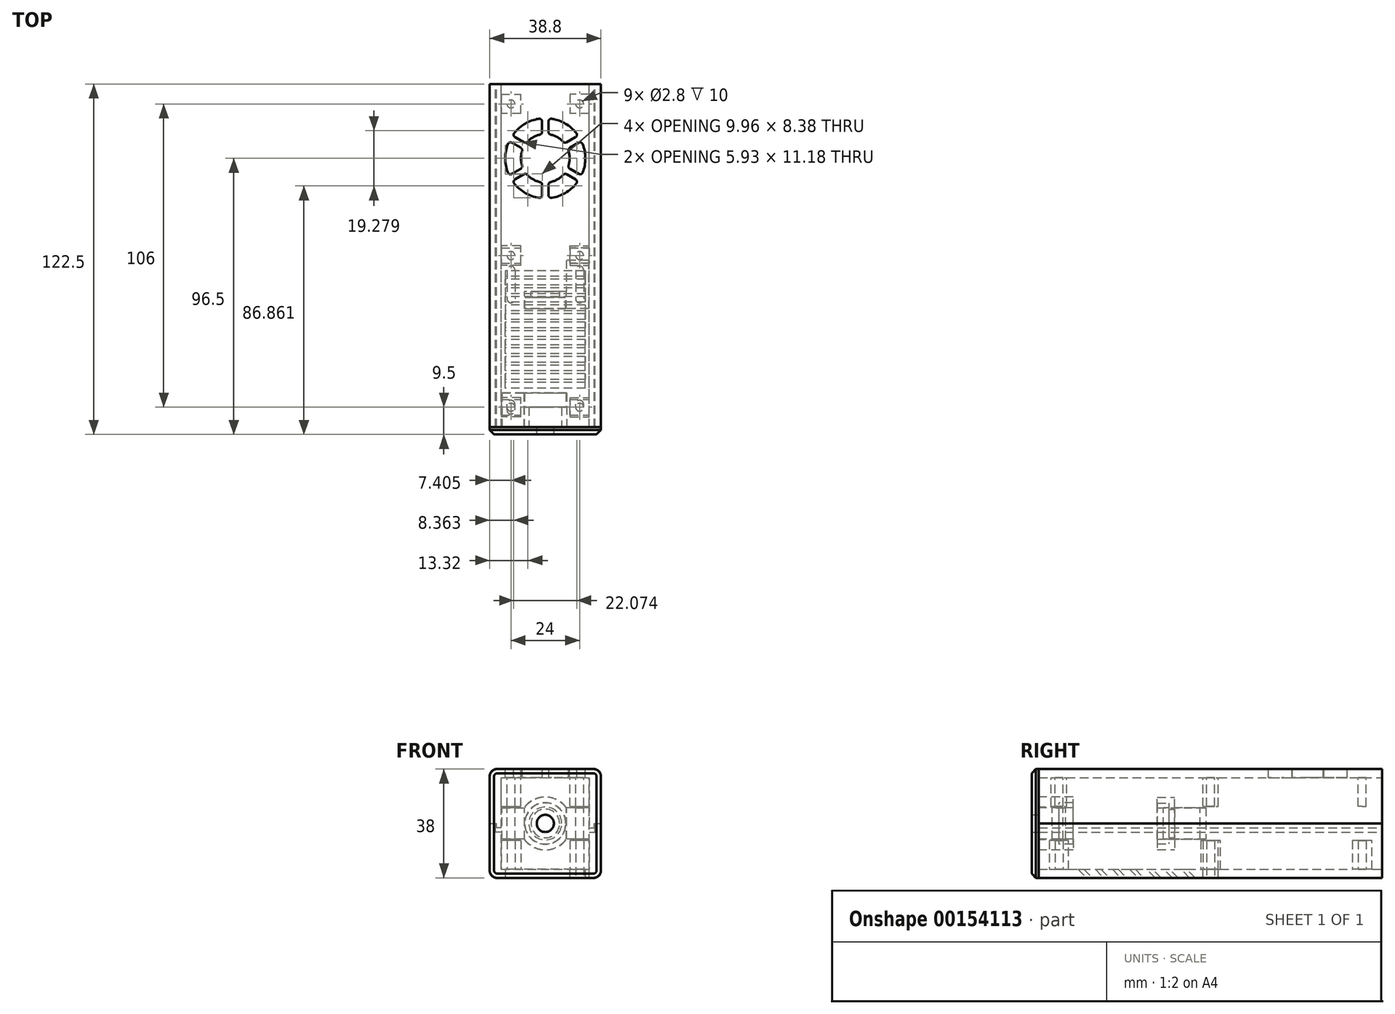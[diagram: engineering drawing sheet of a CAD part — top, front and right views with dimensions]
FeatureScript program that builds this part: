
annotation { "Feature Type Name" : "Feature", "Feature Type Description" : "" }
export const myFeature = defineFeature(function(context is Context, id is Id, definition is map)
    precondition{}
    {
        {
            var Q0;
            Q0=qCreatedBy(makeId("Front.planeOp"),FACE);
            var sketch = newSketch(context, id + "F0", { "sketchPlane" : qUnion([Q0])});
            skLineSegment(sketch, "E0", {"start": v(-19.4, 0) * mm, "end": v(-19.4, -16.6) * mm});
            skLineSegment(sketch, "E1", {"start": v(-17, -19) * mm, "end": v(0, -19) * mm});
            skLineSegment(sketch, "E2", {"start": v(10, -16) * mm, "end": v(-15.4, -16) * mm});
            skLineSegment(sketch, "E3", {"start": v(-15.4, -16) * mm, "end": v(-15.4, -3) * mm});
            skLineSegment(sketch, "E4", {"start": v(-15.4, -3) * mm, "end": v(-17.4, -3) * mm});
            skLineSegment(sketch, "E5", {"start": v(-17.4, -3) * mm, "end": v(-17.4, 0) * mm});
            skPoint(sketch, "E6.visualSharp", {"position": v(-19.4, -19) * mm});
            skArc(sketch, "E6.filletArc", {"start": v(-19.4, -16.6) * mm, "mid": v(-18.7, -18.3) * mm, "end": v(-17, -19) * mm});
            skLineSegment(sketch, "E7.MirrorCS", {"start": v(17.4, 0) * mm, "end": v(19.4, 0) * mm});
            skLineSegment(sketch, "E8.MirrorCS", {"start": v(15.4, -3) * mm, "end": v(17.4, -3) * mm});
            skLineSegment(sketch, "E9.MirrorCS", {"start": v(19.4, 0) * mm, "end": v(19.4, -16.6) * mm});
            skLineSegment(sketch, "E10.MirrorCS", {"start": v(-10, -16) * mm, "end": v(15.4, -16) * mm});
            skLineSegment(sketch, "E11.MirrorCS", {"start": v(17.4, -3) * mm, "end": v(17.4, 0) * mm});
            skLineSegment(sketch, "E12.MirrorCS", {"start": v(15.4, -16) * mm, "end": v(15.4, -3) * mm});
            skLineSegment(sketch, "E13.MirrorCS", {"start": v(17, -19) * mm, "end": v(0, -19) * mm});
            skPoint(sketch, "E14.MirrorP", {"position": v(19.4, -19) * mm});
            skArc(sketch, "E15.MirrorCS", {"start": v(19.4, -16.6) * mm, "mid": v(18.7, -18.3) * mm, "end": v(17, -19) * mm});
            skLineSegment(sketch, "E16.MirrorCS", {"start": v(-17, 19) * mm, "end": v(0, 19) * mm});
            skLineSegment(sketch, "E17.MirrorCS", {"start": v(17, 19) * mm, "end": v(0, 19) * mm});
            skArc(sketch, "E18.MirrorCS", {"start": v(19.4, 16.6) * mm, "mid": v(18.7, 18.3) * mm, "end": v(17, 19) * mm});
            skLineSegment(sketch, "E19.MirrorCS", {"start": v(19.4, 0) * mm, "end": v(19.4, 16.6) * mm});
            skLineSegment(sketch, "E20.MirrorCS", {"start": v(-19.4, 0) * mm, "end": v(-19.4, 16.6) * mm});
            skPoint(sketch, "E21.MirrorP", {"position": v(-19.4, 19) * mm});
            skArc(sketch, "E22.MirrorCS", {"start": v(-19.4, 16.6) * mm, "mid": v(-18.7, 18.3) * mm, "end": v(-17, 19) * mm});
            skLineSegment(sketch, "E23", {"start": v(-19.4, 0) * mm, "end": v(-17.4, 0) * mm});
            skLineSegment(sketch, "E24", {"start": v(-15.4, -1.5) * mm, "end": v(-15.4, 16) * mm});
            skLineSegment(sketch, "E25", {"start": v(-15.4, -1.5) * mm, "end": v(-17.1, -1.5) * mm});
            skLineSegment(sketch, "E26", {"start": v(-17.1, -1.5) * mm, "end": v(-17.1, 0) * mm});
            skLineSegment(sketch, "E27", {"start": v(-17.1, 0) * mm, "end": v(-17.4, 0) * mm});
            skLineSegment(sketch, "E28", {"start": v(-15.4, 16) * mm, "end": v(15.4, 16) * mm});
            skLineSegment(sketch, "E29", {"start": v(15.4, 16) * mm, "end": v(15.4, -1.5) * mm});
            skLineSegment(sketch, "E30", {"start": v(15.4, -1.5) * mm, "end": v(17.1, -1.5) * mm});
            skPoint(sketch, "E30.endSnap0", {"position": v(17.4, -1.5) * mm});
            skLineSegment(sketch, "E31", {"start": v(17.1, -1.5) * mm, "end": v(17.1, 0) * mm});
            skLineSegment(sketch, "E32", {"start": v(17.1, 0) * mm, "end": v(17.4, 0) * mm});
            skSolve(sketch);
        }
        {
            var Q0;
            Q0=makeQuery(id+"F0.imprint","IMPRINT",FACE,{"disambiguationData":[TD([[makeQuery(id+"F0.imprint","IMPRINT",EDGE,{"derivedFrom":sQuery(id+"F0.wireOp",EDGE,"E0")}),1.0]])]});
            var Q1;
            {var subQ0=sQuery(id+"F0.wireOp",EDGE,"Xo03iRkJ-jKT7-Ic2D-cY5B-pt2Z7VC4vIDv");Q1=makeQuery(id+"F0.imprint","IMPRINT",FACE,{"disambiguationData":[TD([[makeQuery(id+"F0.imprint","IMPRINT",EDGE,{"derivedFrom":subQ0}),-1.0]])]});}
            var Q2;
            {var subQ0=sQuery(id+"F0.wireOp",EDGE,"d39963a0-51db-4fea-9cc0-66fd8d7172660.MirrorCS");Q2=makeQuery(id+"F0.imprint","IMPRINT",FACE,{"disambiguationData":[TD([[makeQuery(id+"F0.imprint","IMPRINT",EDGE,{"derivedFrom":subQ0}),1.0]])]});}
            extrude(context, id + "F1", {"entities" : qUnion([Q0, Q1, Q2]), "depth" : 60 * mm, "hasSecondDirection" : true, "secondDirectionOppositeDirection" : true, "secondDirectionDepth" : 60 * mm});
        }
        {
            var Q0;
            Q0=makeQuery(id+"F0.imprint","IMPRINT",FACE,{"disambiguationData":[TD([[makeQuery(id+"F0.imprint","IMPRINT",EDGE,{"derivedFrom":sQuery(id+"F0.wireOp",EDGE,"E7.MirrorCS")}),1.0]])]});
            var Q1;
            {var subQ0=sQuery(id+"F0.wireOp",EDGE,"ff36f887-7d90-4820-9e64-af2514271e780.MirrorCS");Q1=makeQuery(id+"F0.imprint","IMPRINT",FACE,{"disambiguationData":[TD([[makeQuery(id+"F0.imprint","IMPRINT",EDGE,{"derivedFrom":subQ0}),1.0]])]});}
            var Q2;
            {var subQ0=sQuery(id+"F0.wireOp",EDGE,"acc9a72e-b05e-4517-aa3a-cfba1e2fd8f90.MirrorCS");Q2=makeQuery(id+"F0.imprint","IMPRINT",FACE,{"disambiguationData":[TD([[makeQuery(id+"F0.imprint","IMPRINT",EDGE,{"derivedFrom":subQ0}),-1.0]])]});}
            var Q3;
            Q3=makeQuery(id+"F1.opExtrude","CAP_FACE",FACE,{"disambiguationData":[OSD([sQuery(id+"F0.wireOp",EDGE,"E0"),sQuery(id+"F0.wireOp",EDGE,"E1"),sQuery(id+"F0.wireOp",EDGE,"E2"),sQuery(id+"F0.wireOp",EDGE,"E3"),sQuery(id+"F0.wireOp",EDGE,"E4"),sQuery(id+"F0.wireOp",EDGE,"E5"),sQuery(id+"F0.wireOp",EDGE,"E6.filletArc"),sQuery(id+"F0.wireOp",EDGE,"E7.MirrorCS"),sQuery(id+"F0.wireOp",EDGE,"E8.MirrorCS"),sQuery(id+"F0.wireOp",EDGE,"E9.MirrorCS"),sQuery(id+"F0.wireOp",EDGE,"E10.MirrorCS"),sQuery(id+"F0.wireOp",EDGE,"E11.MirrorCS"),sQuery(id+"F0.wireOp",EDGE,"E12.MirrorCS"),sQuery(id+"F0.wireOp",EDGE,"E13.MirrorCS"),sQuery(id+"F0.wireOp",EDGE,"E15.MirrorCS"),sQuery(id+"F0.wireOp",EDGE,"Xo03iRkJ-jKT7-Ic2D-cY5B-pt2Z7VC4vIDv"),sQuery(id+"F0.wireOp",EDGE,"BTEHV5c4-qzld-xg7n-A6UV-d1dODqSnIxqR"),sQuery(id+"F0.wireOp",EDGE,"j2f2Hjq2-E5bA-Y5t0-WPVC-FpMQT2KFEy1b"),sQuery(id+"F0.wireOp",EDGE,"d39963a0-51db-4fea-9cc0-66fd8d7172660.MirrorCS"),sQuery(id+"F0.wireOp",EDGE,"d39963a0-51db-4fea-9cc0-66fd8d7172661.MirrorCS"),sQuery(id+"F0.wireOp",EDGE,"d39963a0-51db-4fea-9cc0-66fd8d7172662.MirrorCS"),sQuery(id+"F0.wireOp",EDGE,"E23")])],"isStart":false});
            var Q4;
            Q4=makeQuery(id+"F1.opExtrude","CAP_FACE",FACE,{"disambiguationData":[OSD([sQuery(id+"F0.wireOp",EDGE,"E0"),sQuery(id+"F0.wireOp",EDGE,"E1"),sQuery(id+"F0.wireOp",EDGE,"E2"),sQuery(id+"F0.wireOp",EDGE,"E3"),sQuery(id+"F0.wireOp",EDGE,"E4"),sQuery(id+"F0.wireOp",EDGE,"E5"),sQuery(id+"F0.wireOp",EDGE,"E6.filletArc"),sQuery(id+"F0.wireOp",EDGE,"E7.MirrorCS"),sQuery(id+"F0.wireOp",EDGE,"E8.MirrorCS"),sQuery(id+"F0.wireOp",EDGE,"E9.MirrorCS"),sQuery(id+"F0.wireOp",EDGE,"E10.MirrorCS"),sQuery(id+"F0.wireOp",EDGE,"E11.MirrorCS"),sQuery(id+"F0.wireOp",EDGE,"E12.MirrorCS"),sQuery(id+"F0.wireOp",EDGE,"E13.MirrorCS"),sQuery(id+"F0.wireOp",EDGE,"E15.MirrorCS"),sQuery(id+"F0.wireOp",EDGE,"Xo03iRkJ-jKT7-Ic2D-cY5B-pt2Z7VC4vIDv"),sQuery(id+"F0.wireOp",EDGE,"BTEHV5c4-qzld-xg7n-A6UV-d1dODqSnIxqR"),sQuery(id+"F0.wireOp",EDGE,"j2f2Hjq2-E5bA-Y5t0-WPVC-FpMQT2KFEy1b"),sQuery(id+"F0.wireOp",EDGE,"d39963a0-51db-4fea-9cc0-66fd8d7172660.MirrorCS"),sQuery(id+"F0.wireOp",EDGE,"d39963a0-51db-4fea-9cc0-66fd8d7172661.MirrorCS"),sQuery(id+"F0.wireOp",EDGE,"d39963a0-51db-4fea-9cc0-66fd8d7172662.MirrorCS"),sQuery(id+"F0.wireOp",EDGE,"E23")])],"isStart":true});
            extrude(context, id + "F2", {"entities" : qUnion([Q0, Q1, Q2]), "endBound" : BoundingType.UP_TO_SURFACE, "endBoundEntityFace" : qUnion([Q3]), "depth" : 25 * mm, "hasSecondDirection" : true, "secondDirectionBound" : SecondDirectionBoundingType.UP_TO_SURFACE, "secondDirectionOppositeDirection" : true, "secondDirectionBoundEntityFace" : qUnion([Q4]), "secondDirectionDepth" : 25 * mm});
        }
        {
            var Q0;
            {var subQ0=sQuery(id+"F0.wireOp",EDGE,"E10.MirrorCS");Q0=makeQuery(id+"F1.opExtrude","SWEPT_FACE",FACE,{"disambiguationData":[OSD([subQ0]),TDD([makeQuery(id+"F0.imprint","IMPRINT",EDGE,{"disambiguationData":[TD([[makeQuery(id+"F0.imprint","INTERSECT",VERTEX,{"derivedFrom":[subQ0,sQuery(id+"F0.wireOp",EDGE,"E12.MirrorCS")]}),1.0]])],"derivedFrom":subQ0})])]});}
            cPlane(context, id + "F3", {"entities" : qUnion([Q0]), "cplaneType" : CPlaneType.OFFSET, "offset" : 0 * mm, "width" : 150 * mm, "height" : 150 * mm});
        }
        {
            var Q0;
            Q0=qCreatedBy(id+"F3.planeOp",FACE);
            var sketch = newSketch(context, id + "F4", { "sketchPlane" : qUnion([Q0])});
            skLineSegment(sketch, "E33", {"start": v(10.01, 0) * mm, "end": v(15.4, 0) * mm, "construction": true});
            skLineSegment(sketch, "E34.bottom", {"start": v(15.4, 2.7) * mm, "end": v(10, 2.7) * mm});
            skLineSegment(sketch, "E34.top", {"start": v(15.4, -2.7) * mm, "end": v(10, -2.7) * mm});
            skLineSegment(sketch, "E34.left", {"start": v(15.4, 2.7) * mm, "end": v(15.4, -2.7) * mm});
            skPoint(sketch, "E34.middle", {"position": v(12, 0) * mm});
            skCircle(sketch, "E35", {"center": v(12, 0) * mm, "radius": 1.4 * mm});
            skLineSegment(sketch, "E36.MirrorCS", {"start": v(15.4, -2.7) * mm, "end": v(15.4, 2.7) * mm});
            skLineSegment(sketch, "E37.bottom", {"start": v(10, 2.7) * mm, "end": v(8.6, 2.7) * mm});
            skLineSegment(sketch, "E37.top", {"start": v(10, -2.7) * mm, "end": v(8.6, -2.7) * mm});
            skLineSegment(sketch, "E37.right", {"start": v(8.6, 2.7) * mm, "end": v(8.6, -2.7) * mm});
            skPoint(sketch, "E38.0.1.0", {"position": v(12, 53) * mm});
            skLineSegment(sketch, "E38.0.1.1", {"start": v(10.01, 53) * mm, "end": v(15.4, 53) * mm, "construction": true});
            skCircle(sketch, "E38.0.1.2", {"center": v(12, 53) * mm, "radius": 1.4 * mm});
            skLineSegment(sketch, "E38.0.1.3", {"start": v(15.4, 55.7) * mm, "end": v(10, 55.7) * mm});
            skLineSegment(sketch, "E38.0.1.4", {"start": v(15.4, 50.3) * mm, "end": v(15.4, 55.7) * mm});
            skLineSegment(sketch, "E38.0.1.5", {"start": v(8.6, 55.7) * mm, "end": v(8.6, 50.3) * mm});
            skPoint(sketch, "E38.0.1.6", {"position": v(12, 53) * mm});
            skLineSegment(sketch, "E38.0.1.7", {"start": v(15.4, 55.7) * mm, "end": v(10, 55.7) * mm});
            skLineSegment(sketch, "E38.0.1.8", {"start": v(15.4, 55.7) * mm, "end": v(15.4, 50.3) * mm});
            skCircle(sketch, "E38.0.1.9", {"center": v(12, 53) * mm, "radius": 1.4 * mm});
            skLineSegment(sketch, "E38.0.1.10", {"start": v(15.4, 50.3) * mm, "end": v(10, 50.3) * mm});
            skLineSegment(sketch, "E38.0.1.11", {"start": v(15.4, 50.3) * mm, "end": v(10, 50.3) * mm});
            skLineSegment(sketch, "E38.0.1.12", {"start": v(10, 55.7) * mm, "end": v(8.6, 55.7) * mm});
            skLineSegment(sketch, "E38.0.1.13", {"start": v(10, 50.3) * mm, "end": v(8.6, 50.3) * mm});
            skPoint(sketch, "E38.1.0.0", {"position": v(-12, 0) * mm});
            skLineSegment(sketch, "E38.1.0.1", {"start": v(-13.99, 0) * mm, "end": v(-8.6, 0) * mm, "construction": true});
            skCircle(sketch, "E38.1.0.2", {"center": v(-12, 0) * mm, "radius": 1.4 * mm});
            skLineSegment(sketch, "E38.1.0.3", {"start": v(-8.6, 2.7) * mm, "end": v(-14, 2.7) * mm});
            skLineSegment(sketch, "E38.1.0.4", {"start": v(-8.6, -2.7) * mm, "end": v(-8.6, 2.7) * mm});
            skLineSegment(sketch, "E38.1.0.5", {"start": v(-15.4, 2.7) * mm, "end": v(-15.4, -2.7) * mm});
            skPoint(sketch, "E38.1.0.6", {"position": v(-12, 0) * mm});
            skLineSegment(sketch, "E38.1.0.7", {"start": v(-8.6, 2.7) * mm, "end": v(-14, 2.7) * mm});
            skLineSegment(sketch, "E38.1.0.8", {"start": v(-8.6, 2.7) * mm, "end": v(-8.6, -2.7) * mm});
            skCircle(sketch, "E38.1.0.9", {"center": v(-12, 0) * mm, "radius": 1.4 * mm});
            skLineSegment(sketch, "E38.1.0.10", {"start": v(-8.6, -2.7) * mm, "end": v(-14, -2.7) * mm});
            skLineSegment(sketch, "E38.1.0.11", {"start": v(-8.6, -2.7) * mm, "end": v(-14, -2.7) * mm});
            skLineSegment(sketch, "E38.1.0.12", {"start": v(-14, 2.7) * mm, "end": v(-15.4, 2.7) * mm});
            skLineSegment(sketch, "E38.1.0.13", {"start": v(-14, -2.7) * mm, "end": v(-15.4, -2.7) * mm});
            skPoint(sketch, "E38.1.1.0", {"position": v(-12, 53) * mm});
            skLineSegment(sketch, "E38.1.1.1", {"start": v(-13.99, 53) * mm, "end": v(-8.6, 53) * mm, "construction": true});
            skCircle(sketch, "E38.1.1.2", {"center": v(-12, 53) * mm, "radius": 1.4 * mm});
            skLineSegment(sketch, "E38.1.1.3", {"start": v(-8.6, 55.7) * mm, "end": v(-14, 55.7) * mm});
            skLineSegment(sketch, "E38.1.1.4", {"start": v(-8.6, 50.3) * mm, "end": v(-8.6, 55.7) * mm});
            skLineSegment(sketch, "E38.1.1.5", {"start": v(-15.4, 55.7) * mm, "end": v(-15.4, 50.3) * mm});
            skPoint(sketch, "E38.1.1.6", {"position": v(-12, 53) * mm});
            skLineSegment(sketch, "E38.1.1.7", {"start": v(-8.6, 55.7) * mm, "end": v(-14, 55.7) * mm});
            skLineSegment(sketch, "E38.1.1.8", {"start": v(-8.6, 55.7) * mm, "end": v(-8.6, 50.3) * mm});
            skCircle(sketch, "E38.1.1.9", {"center": v(-12, 53) * mm, "radius": 1.4 * mm});
            skLineSegment(sketch, "E38.1.1.10", {"start": v(-8.6, 50.3) * mm, "end": v(-14, 50.3) * mm});
            skLineSegment(sketch, "E38.1.1.11", {"start": v(-8.6, 50.3) * mm, "end": v(-14, 50.3) * mm});
            skLineSegment(sketch, "E38.1.1.12", {"start": v(-14, 55.7) * mm, "end": v(-15.4, 55.7) * mm});
            skLineSegment(sketch, "E38.1.1.13", {"start": v(-14, 50.3) * mm, "end": v(-15.4, 50.3) * mm});
            skLineSegment(sketch, "E38.direction1", {"start": v(8.6, -2.7) * mm, "end": v(-15.4, -2.7) * mm, "construction": true});
            skLineSegment(sketch, "E38.direction2", {"start": v(8.6, -2.7) * mm, "end": v(8.6, 50.3) * mm, "construction": true});
            skPoint(sketch, "E39.0.1.0", {"position": v(12, -53) * mm});
            skLineSegment(sketch, "E39.0.1.1", {"start": v(8.6, -55.7) * mm, "end": v(-15.4, -55.7) * mm, "construction": true});
            skPoint(sketch, "E39.0.1.2", {"position": v(-12, -53) * mm});
            skPoint(sketch, "E39.0.1.3", {"position": v(12, -53) * mm});
            skPoint(sketch, "E39.0.1.4", {"position": v(-12, -53) * mm});
            skLineSegment(sketch, "E39.0.1.5", {"start": v(-14, -55.7) * mm, "end": v(-15.4, -55.7) * mm});
            skLineSegment(sketch, "E39.0.1.6", {"start": v(8.6, -50.3) * mm, "end": v(8.6, -55.7) * mm});
            skLineSegment(sketch, "E39.0.1.7", {"start": v(-8.6, -55.7) * mm, "end": v(-14, -55.7) * mm});
            skLineSegment(sketch, "E39.0.1.8", {"start": v(-15.4, -50.3) * mm, "end": v(-15.4, -55.7) * mm});
            skLineSegment(sketch, "E39.0.1.9", {"start": v(15.4, -55.7) * mm, "end": v(10, -55.7) * mm});
            skLineSegment(sketch, "E39.0.1.10", {"start": v(15.4, -50.3) * mm, "end": v(10, -50.3) * mm});
            skLineSegment(sketch, "E39.0.1.11", {"start": v(-14, -50.3) * mm, "end": v(-15.4, -50.3) * mm});
            skLineSegment(sketch, "E39.0.1.12", {"start": v(10.01, -53) * mm, "end": v(15.4, -53) * mm, "construction": true});
            skCircle(sketch, "E39.0.1.13", {"center": v(12, -53) * mm, "radius": 1.4 * mm});
            skLineSegment(sketch, "E39.0.1.14", {"start": v(15.4, -55.7) * mm, "end": v(15.4, -50.3) * mm});
            skLineSegment(sketch, "E39.0.1.15", {"start": v(10, -50.3) * mm, "end": v(8.6, -50.3) * mm});
            skLineSegment(sketch, "E39.0.1.16", {"start": v(10, -55.7) * mm, "end": v(8.6, -55.7) * mm});
            skLineSegment(sketch, "E39.0.1.17", {"start": v(-8.6, -55.7) * mm, "end": v(-8.6, -50.3) * mm});
            skLineSegment(sketch, "E39.0.1.18", {"start": v(-8.6, -50.3) * mm, "end": v(-14, -50.3) * mm});
            skLineSegment(sketch, "E39.0.1.19", {"start": v(-13.99, -53) * mm, "end": v(-8.6, -53) * mm, "construction": true});
            skLineSegment(sketch, "E39.0.1.20", {"start": v(-8.6, -55.7) * mm, "end": v(-14, -55.7) * mm});
            skCircle(sketch, "E39.0.1.21", {"center": v(-12, -53) * mm, "radius": 1.4 * mm});
            skLineSegment(sketch, "E39.0.1.22", {"start": v(-8.6, -50.3) * mm, "end": v(-14, -50.3) * mm});
            skLineSegment(sketch, "E39.0.1.23", {"start": v(15.4, -50.3) * mm, "end": v(10, -50.3) * mm});
            skLineSegment(sketch, "E39.0.1.24", {"start": v(15.4, -55.7) * mm, "end": v(10, -55.7) * mm});
            skLineSegment(sketch, "E39.0.1.25", {"start": v(15.4, -50.3) * mm, "end": v(15.4, -55.7) * mm});
            skCircle(sketch, "E39.0.1.26", {"center": v(12, -53) * mm, "radius": 1.4 * mm});
            skLineSegment(sketch, "E39.0.1.27", {"start": v(-8.6, -50.3) * mm, "end": v(-8.6, -55.7) * mm});
            skCircle(sketch, "E39.0.1.28", {"center": v(-12, -53) * mm, "radius": 1.4 * mm});
            skLineSegment(sketch, "E39.direction1", {"start": v(-15.4, -2.7) * mm, "end": v(74.5, -2.7) * mm, "construction": true});
            skLineSegment(sketch, "E39.direction2", {"start": v(-15.4, -2.7) * mm, "end": v(-15.4, -55.7) * mm, "construction": true});
            skLineSegment(sketch, "E40.bottom", {"start": v(-8.6, 2.7) * mm, "end": v(-15.4, 2.7) * mm});
            skLineSegment(sketch, "E40.top", {"start": v(-8.6, 3.4) * mm, "end": v(-15.4, 3.4) * mm});
            skLineSegment(sketch, "E40.left", {"start": v(-8.6, 2.7) * mm, "end": v(-8.6, 3.4) * mm});
            skLineSegment(sketch, "E40.right", {"start": v(-15.4, 2.7) * mm, "end": v(-15.4, 3.4) * mm});
            skLineSegment(sketch, "E41.bottom", {"start": v(-8.6, -2.7) * mm, "end": v(-15.4, -2.7) * mm});
            skLineSegment(sketch, "E41.top", {"start": v(-8.6, -3.4) * mm, "end": v(-15.4, -3.4) * mm});
            skLineSegment(sketch, "E41.left", {"start": v(-8.6, -2.7) * mm, "end": v(-8.6, -3.4) * mm});
            skLineSegment(sketch, "E41.right", {"start": v(-15.4, -2.7) * mm, "end": v(-15.4, -3.4) * mm});
            skLineSegment(sketch, "E42.bottom", {"start": v(8.6, -2.7) * mm, "end": v(15.4, -2.7) * mm});
            skLineSegment(sketch, "E42.top", {"start": v(8.6, -3.4) * mm, "end": v(15.4, -3.4) * mm});
            skLineSegment(sketch, "E42.left", {"start": v(8.6, -2.7) * mm, "end": v(8.6, -3.4) * mm});
            skLineSegment(sketch, "E42.right", {"start": v(15.4, -2.7) * mm, "end": v(15.4, -3.4) * mm});
            skLineSegment(sketch, "E43.bottom", {"start": v(8.6, 2.7) * mm, "end": v(15.4, 2.7) * mm});
            skLineSegment(sketch, "E43.top", {"start": v(8.6, 3.4) * mm, "end": v(15.4, 3.4) * mm});
            skLineSegment(sketch, "E43.left", {"start": v(8.6, 2.7) * mm, "end": v(8.6, 3.4) * mm});
            skLineSegment(sketch, "E43.right", {"start": v(15.4, 2.7) * mm, "end": v(15.4, 3.4) * mm});
            skLineSegment(sketch, "E44.bottom", {"start": v(-8.6, 50.3) * mm, "end": v(-15.4, 50.3) * mm});
            skLineSegment(sketch, "E44.top", {"start": v(-8.6, 49.6) * mm, "end": v(-15.4, 49.6) * mm});
            skLineSegment(sketch, "E44.left", {"start": v(-8.6, 50.3) * mm, "end": v(-8.6, 49.6) * mm});
            skLineSegment(sketch, "E44.right", {"start": v(-15.4, 50.3) * mm, "end": v(-15.4, 49.6) * mm});
            skLineSegment(sketch, "E45.bottom", {"start": v(15.4, 50.3) * mm, "end": v(8.6, 50.3) * mm});
            skLineSegment(sketch, "E45.top", {"start": v(15.4, 49.6) * mm, "end": v(8.6, 49.6) * mm});
            skLineSegment(sketch, "E45.left", {"start": v(15.4, 50.3) * mm, "end": v(15.4, 49.6) * mm});
            skLineSegment(sketch, "E45.right", {"start": v(8.6, 50.3) * mm, "end": v(8.6, 49.6) * mm});
            skLineSegment(sketch, "E46.bottom", {"start": v(15.4, 55.7) * mm, "end": v(8.6, 55.7) * mm});
            skLineSegment(sketch, "E46.top", {"start": v(15.4, 56.4) * mm, "end": v(8.6, 56.4) * mm});
            skLineSegment(sketch, "E46.left", {"start": v(15.4, 55.7) * mm, "end": v(15.4, 56.4) * mm});
            skLineSegment(sketch, "E46.right", {"start": v(8.6, 55.7) * mm, "end": v(8.6, 56.4) * mm});
            skLineSegment(sketch, "E47.bottom", {"start": v(-15.4, 55.7) * mm, "end": v(-8.6, 55.7) * mm});
            skLineSegment(sketch, "E47.top", {"start": v(-15.4, 56.4) * mm, "end": v(-8.6, 56.4) * mm});
            skLineSegment(sketch, "E47.left", {"start": v(-15.4, 55.7) * mm, "end": v(-15.4, 56.4) * mm});
            skLineSegment(sketch, "E47.right", {"start": v(-8.6, 55.7) * mm, "end": v(-8.6, 56.4) * mm});
            skLineSegment(sketch, "E48.bottom", {"start": v(-8.6, -50.3) * mm, "end": v(-15.4, -50.3) * mm});
            skLineSegment(sketch, "E48.top", {"start": v(-8.6, -49.6) * mm, "end": v(-15.4, -49.6) * mm});
            skLineSegment(sketch, "E48.left", {"start": v(-8.6, -50.3) * mm, "end": v(-8.6, -49.6) * mm});
            skLineSegment(sketch, "E48.right", {"start": v(-15.4, -50.3) * mm, "end": v(-15.4, -49.6) * mm});
            skLineSegment(sketch, "E49.bottom", {"start": v(-8.6, -55.7) * mm, "end": v(-15.4, -55.7) * mm});
            skLineSegment(sketch, "E49.top", {"start": v(-8.6, -56.4) * mm, "end": v(-15.4, -56.4) * mm});
            skLineSegment(sketch, "E49.left", {"start": v(-8.6, -55.7) * mm, "end": v(-8.6, -56.4) * mm});
            skLineSegment(sketch, "E49.right", {"start": v(-15.4, -55.7) * mm, "end": v(-15.4, -56.4) * mm});
            skLineSegment(sketch, "E50.bottom", {"start": v(8.6, -55.7) * mm, "end": v(15.4, -55.7) * mm});
            skLineSegment(sketch, "E50.top", {"start": v(8.6, -56.4) * mm, "end": v(15.4, -56.4) * mm});
            skLineSegment(sketch, "E50.left", {"start": v(8.6, -55.7) * mm, "end": v(8.6, -56.4) * mm});
            skLineSegment(sketch, "E50.right", {"start": v(15.4, -55.7) * mm, "end": v(15.4, -56.4) * mm});
            skLineSegment(sketch, "E51.bottom", {"start": v(8.6, -50.3) * mm, "end": v(15.4, -50.3) * mm});
            skLineSegment(sketch, "E51.top", {"start": v(8.6, -49.6) * mm, "end": v(15.4, -49.6) * mm});
            skLineSegment(sketch, "E51.left", {"start": v(8.6, -50.3) * mm, "end": v(8.6, -49.6) * mm});
            skLineSegment(sketch, "E51.right", {"start": v(15.4, -50.3) * mm, "end": v(15.4, -49.6) * mm});
            skSolve(sketch);
        }
        {
            var Q0;
            Q0=makeQuery(id+"F4.imprint","IMPRINT",FACE,{"disambiguationData":[TD([[makeQuery(id+"F4.imprint","IMPRINT",EDGE,{"derivedFrom":sQuery(id+"F4.wireOp",EDGE,"E35")}),1.0]])]});
            var Q1;
            Q1=makeQuery(id+"F4.imprint","IMPRINT",FACE,{"disambiguationData":[TD([[makeQuery(id+"F4.imprint","IMPRINT",EDGE,{"derivedFrom":sQuery(id+"F4.wireOp",EDGE,"E38.1.0.5")}),1.0]])]});
            var Q2;
            Q2=makeQuery(id+"F4.imprint","IMPRINT",FACE,{"disambiguationData":[TD([[makeQuery(id+"F4.imprint","IMPRINT",EDGE,{"derivedFrom":sQuery(id+"F4.wireOp",EDGE,"E38.0.1.5")}),1.0]])]});
            var Q3;
            Q3=makeQuery(id+"F4.imprint","IMPRINT",FACE,{"disambiguationData":[TD([[makeQuery(id+"F4.imprint","IMPRINT",EDGE,{"derivedFrom":sQuery(id+"F4.wireOp",EDGE,"E38.1.1.5")}),1.0]])]});
            var Q4;
            Q4=makeQuery(id+"F4.imprint","IMPRINT",FACE,{"disambiguationData":[TD([[makeQuery(id+"F4.imprint","IMPRINT",EDGE,{"derivedFrom":sQuery(id+"F4.wireOp",EDGE,"E39.0.1.5")}),-1.0]])]});
            var Q5;
            Q5=makeQuery(id+"F4.imprint","IMPRINT",FACE,{"disambiguationData":[TD([[makeQuery(id+"F4.imprint","IMPRINT",EDGE,{"derivedFrom":sQuery(id+"F4.wireOp",EDGE,"E39.0.1.6")}),1.0]])]});
            var Q6;
            Q6=makeQuery(id+"F4.imprint","IMPRINT",FACE,{"disambiguationData":[TD([[makeQuery(id+"F4.imprint","IMPRINT",EDGE,{"derivedFrom":sQuery(id+"F4.wireOp",EDGE,"E41.top")}),-1.0]])]});
            var Q7;
            Q7=makeQuery(id+"F4.imprint","IMPRINT",FACE,{"disambiguationData":[TD([[makeQuery(id+"F4.imprint","IMPRINT",EDGE,{"derivedFrom":sQuery(id+"F4.wireOp",EDGE,"E40.top")}),1.0]])]});
            var Q8;
            Q8=makeQuery(id+"F4.imprint","IMPRINT",FACE,{"disambiguationData":[TD([[makeQuery(id+"F4.imprint","IMPRINT",EDGE,{"derivedFrom":sQuery(id+"F4.wireOp",EDGE,"E43.top")}),-1.0]])]});
            var Q9;
            Q9=makeQuery(id+"F4.imprint","IMPRINT",FACE,{"disambiguationData":[TD([[makeQuery(id+"F4.imprint","IMPRINT",EDGE,{"derivedFrom":sQuery(id+"F4.wireOp",EDGE,"E42.top")}),1.0]])]});
            var Q10;
            Q10=makeQuery(id+"F4.imprint","IMPRINT",FACE,{"disambiguationData":[TD([[makeQuery(id+"F4.imprint","IMPRINT",EDGE,{"derivedFrom":sQuery(id+"F4.wireOp",EDGE,"E47.top")}),-1.0]])]});
            var Q11;
            Q11=makeQuery(id+"F4.imprint","IMPRINT",FACE,{"disambiguationData":[TD([[makeQuery(id+"F4.imprint","IMPRINT",EDGE,{"derivedFrom":sQuery(id+"F4.wireOp",EDGE,"E44.top")}),-1.0]])]});
            var Q12;
            Q12=makeQuery(id+"F4.imprint","IMPRINT",FACE,{"disambiguationData":[TD([[makeQuery(id+"F4.imprint","IMPRINT",EDGE,{"derivedFrom":sQuery(id+"F4.wireOp",EDGE,"E45.top")}),-1.0]])]});
            var Q13;
            Q13=makeQuery(id+"F4.imprint","IMPRINT",FACE,{"disambiguationData":[TD([[makeQuery(id+"F4.imprint","IMPRINT",EDGE,{"derivedFrom":sQuery(id+"F4.wireOp",EDGE,"E46.top")}),1.0]])]});
            var Q14;
            Q14=makeQuery(id+"F4.imprint","IMPRINT",FACE,{"disambiguationData":[TD([[makeQuery(id+"F4.imprint","IMPRINT",EDGE,{"derivedFrom":sQuery(id+"F4.wireOp",EDGE,"E48.top")}),1.0]])]});
            var Q15;
            {var subQ4=sQuery(id+"F4.wireOp",EDGE,"E39.0.1.8");Q15=makeQuery(id+"F4.imprint","IMPRINT",FACE,{"disambiguationData":[TD([[makeQuery(id+"F4.imprint","IMPRINT",EDGE,{"derivedFrom":subQ4}),1.0]])]});}
            var Q16;
            Q16=makeQuery(id+"F4.imprint","IMPRINT",FACE,{"disambiguationData":[TD([[makeQuery(id+"F4.imprint","IMPRINT",EDGE,{"derivedFrom":sQuery(id+"F4.wireOp",EDGE,"E49.top")}),-1.0]])]});
            var Q17;
            Q17=makeQuery(id+"F4.imprint","IMPRINT",FACE,{"disambiguationData":[TD([[makeQuery(id+"F4.imprint","IMPRINT",EDGE,{"derivedFrom":sQuery(id+"F4.wireOp",EDGE,"E50.top")}),1.0]])]});
            var Q18;
            Q18=makeQuery(id+"F4.imprint","IMPRINT",FACE,{"disambiguationData":[TD([[makeQuery(id+"F4.imprint","IMPRINT",EDGE,{"derivedFrom":sQuery(id+"F4.wireOp",EDGE,"E51.top")}),-1.0]])]});
            extrude(context, id + "F5", {"entities" : qUnion([Q0, Q1, Q2, Q3, Q4, Q5, Q6, Q7, Q8, Q9, Q10, Q11, Q12, Q13, Q14, Q15, Q16, Q17, Q18]), "operationType" : NewBodyOperationType.ADD, "depth" : 10 * mm});
        }
        {
            var Q0;
            {var subQ2=sQuery(id+"F0.wireOp",EDGE,"BTEHV5c4-qzld-xg7n-A6UV-d1dODqSnIxqR");var subQ4=sQuery(id+"F0.wireOp",EDGE,"E12.MirrorCS");var subQ5=sQuery(id+"F0.wireOp",EDGE,"E10.MirrorCS");var subQ7=sQuery(id+"F0.wireOp",EDGE,"E2");Q0=makeQuery(id+"F5oqtaTRLiZ5Fdx_2.boolean.opBoolean","MERGE",FACE,{"derivedFrom":[makeQuery(id+"F1.opExtrude","SWEPT_FACE",FACE,{"disambiguationData":[OSD([subQ5]),TDD([makeQuery(id+"F0.imprint","IMPRINT",EDGE,{"disambiguationData":[TD([[makeQuery(id+"F0.imprint","INTERSECT",VERTEX,{"derivedFrom":[subQ5,subQ2]}),-1.0]])],"derivedFrom":subQ5})])]}),makeQuery(id+"F5.boolean.opBoolean","SPLIT",FACE,{"disambiguationData":[TD([makeQuery(id+"F5.opExtrude","SWEPT_FACE",FACE,{"disambiguationData":[OSD([sQuery(id+"F4.wireOp",EDGE,"7fa35dff-bbc5-4327-865b-78e916851ba6.0.1.24")])]})])],"derivedFrom":makeQuery(id+"F1.opExtrude","SWEPT_FACE",FACE,{"disambiguationData":[OSD([subQ7])]})}),makeQuery(id+"F5.boolean.opBoolean","SPLIT",FACE,{"disambiguationData":[TD([makeQuery(id+"F5.opExtrude","SWEPT_FACE",FACE,{"disambiguationData":[OSD([sQuery(id+"F4.wireOp",EDGE,"7fa35dff-bbc5-4327-865b-78e916851ba6.0.1.18")])]})])],"derivedFrom":makeQuery(id+"F1.opExtrude","SWEPT_FACE",FACE,{"disambiguationData":[OSD([subQ5]),TDD([makeQuery(id+"F0.imprint","IMPRINT",EDGE,{"disambiguationData":[TD([[makeQuery(id+"F0.imprint","INTERSECT",VERTEX,{"derivedFrom":[subQ5,subQ4]}),1.0]])],"derivedFrom":subQ5})])]})}),makeQuery(id+"F5oqtaTRLiZ5Fdx_2.opExtrude","SWEPT_FACE",FACE,{"disambiguationData":[OSD([sQuery(id+"FQpaSjsVbLHPvn0_2.wireOp",EDGE,"tlB3wlaz-5kT3-gLk7-Q1Ps-73qS5PyYQGVd.top")])]})]});}
            var sketch = newSketch(context, id + "F6", { "sketchPlane" : qUnion([Q0])});
            skLineSegment(sketch, "E52.bottom", {"start": v(14, -46.3) * mm, "end": v(-14, -46.3) * mm});
            skLineSegment(sketch, "E52.top", {"start": v(14, -44.3) * mm, "end": v(-14, -44.3) * mm});
            skLineSegment(sketch, "E52.left", {"start": v(14, -46.3) * mm, "end": v(14, -44.3) * mm});
            skLineSegment(sketch, "E52.right", {"start": v(-14, -46.3) * mm, "end": v(-14, -44.3) * mm});
            skPoint(sketch, "E52.middle", {"position": v(0, -45.3) * mm});
            skLineSegment(sketch, "E53.0.1.0", {"start": v(-14, -40.3) * mm, "end": v(-14, -38.3) * mm});
            skLineSegment(sketch, "E53.0.1.1", {"start": v(14, -38.3) * mm, "end": v(-14, -38.3) * mm});
            skLineSegment(sketch, "E53.0.1.2", {"start": v(14, -40.3) * mm, "end": v(-14, -40.3) * mm});
            skLineSegment(sketch, "E53.0.1.3", {"start": v(14, -40.3) * mm, "end": v(14, -38.3) * mm});
            skLineSegment(sketch, "E53.0.2.0", {"start": v(-14, -34.3) * mm, "end": v(-14, -32.3) * mm});
            skLineSegment(sketch, "E53.0.2.1", {"start": v(14, -32.3) * mm, "end": v(-14, -32.3) * mm});
            skLineSegment(sketch, "E53.0.2.2", {"start": v(14, -34.3) * mm, "end": v(-14, -34.3) * mm});
            skLineSegment(sketch, "E53.0.2.3", {"start": v(14, -34.3) * mm, "end": v(14, -32.3) * mm});
            skLineSegment(sketch, "E53.0.3.0", {"start": v(-14, -28.3) * mm, "end": v(-14, -26.3) * mm});
            skLineSegment(sketch, "E53.0.3.1", {"start": v(14, -26.3) * mm, "end": v(-14, -26.3) * mm});
            skLineSegment(sketch, "E53.0.3.2", {"start": v(14, -28.3) * mm, "end": v(-14, -28.3) * mm});
            skLineSegment(sketch, "E53.0.3.3", {"start": v(14, -28.3) * mm, "end": v(14, -26.3) * mm});
            skLineSegment(sketch, "E53.0.4.0", {"start": v(-14, -22.3) * mm, "end": v(-14, -20.3) * mm});
            skLineSegment(sketch, "E53.0.4.1", {"start": v(14, -20.3) * mm, "end": v(-14, -20.3) * mm});
            skLineSegment(sketch, "E53.0.4.2", {"start": v(14, -22.3) * mm, "end": v(-14, -22.3) * mm});
            skLineSegment(sketch, "E53.0.4.3", {"start": v(14, -22.3) * mm, "end": v(14, -20.3) * mm});
            skLineSegment(sketch, "E53.0.5.0", {"start": v(-14, -16.3) * mm, "end": v(-14, -14.3) * mm});
            skLineSegment(sketch, "E53.0.5.1", {"start": v(14, -14.3) * mm, "end": v(-14, -14.3) * mm});
            skLineSegment(sketch, "E53.0.5.2", {"start": v(14, -16.3) * mm, "end": v(-14, -16.3) * mm});
            skLineSegment(sketch, "E53.0.5.3", {"start": v(14, -16.3) * mm, "end": v(14, -14.3) * mm});
            skLineSegment(sketch, "E53.direction1", {"start": v(-14, -46.3) * mm, "end": v(11, -46.3) * mm, "construction": true});
            skLineSegment(sketch, "E53.direction2", {"start": v(-14, -46.3) * mm, "end": v(-14, -40.3) * mm, "construction": true});
            skLineSegment(sketch, "E54.0.0.6", {"start": v(-14, -10.3) * mm, "end": v(-14, -8.3) * mm});
            skLineSegment(sketch, "E54.3.0.6", {"start": v(14, -8.3) * mm, "end": v(-14, -8.3) * mm});
            skLineSegment(sketch, "E54.6.0.6", {"start": v(14, -10.3) * mm, "end": v(-14, -10.3) * mm});
            skLineSegment(sketch, "E54.9.0.6", {"start": v(14, -10.3) * mm, "end": v(14, -8.3) * mm});
            skSolve(sketch);
        }
        {
            var Q0;
            Q0=makeQuery(id+"F1.opExtrude","SWEPT_FACE",FACE,{"disambiguationData":[OSD([sQuery(id+"F0.wireOp",EDGE,"E1"),sQuery(id+"F0.wireOp",EDGE,"E13.MirrorCS")])]});
            var sketch = newSketch(context, id + "F7", { "sketchPlane" : qUnion([Q0])});
            skLineSegment(sketch, "E55", {"start": v(0, 69.46) * mm, "end": v(0, 60) * mm, "construction": true});
            skPoint(sketch, "E55.endSnap0", {"position": v(0, 60) * mm});
            skLineSegment(sketch, "E56.bottom", {"start": v(14, 41.3) * mm, "end": v(-14, 41.3) * mm});
            skLineSegment(sketch, "E56.top", {"start": v(14, 43.3) * mm, "end": v(-14, 43.3) * mm});
            skLineSegment(sketch, "E56.left", {"start": v(14, 41.3) * mm, "end": v(14, 43.3) * mm});
            skLineSegment(sketch, "E56.right", {"start": v(-14, 41.3) * mm, "end": v(-14, 43.3) * mm});
            skPoint(sketch, "E56.middle", {"position": v(0, 42.3) * mm});
            skLineSegment(sketch, "E57.0.1.0", {"start": v(14, 37.3) * mm, "end": v(-14, 37.3) * mm});
            skLineSegment(sketch, "E57.0.1.1", {"start": v(-14, 35.3) * mm, "end": v(-14, 37.3) * mm});
            skLineSegment(sketch, "E57.0.1.2", {"start": v(14, 35.3) * mm, "end": v(-14, 35.3) * mm});
            skLineSegment(sketch, "E57.0.1.3", {"start": v(14, 35.3) * mm, "end": v(14, 37.3) * mm});
            skLineSegment(sketch, "E57.0.2.0", {"start": v(14, 31.3) * mm, "end": v(-14, 31.3) * mm});
            skLineSegment(sketch, "E57.0.2.1", {"start": v(-14, 29.3) * mm, "end": v(-14, 31.3) * mm});
            skLineSegment(sketch, "E57.0.2.2", {"start": v(14, 29.3) * mm, "end": v(-14, 29.3) * mm});
            skLineSegment(sketch, "E57.0.2.3", {"start": v(14, 29.3) * mm, "end": v(14, 31.3) * mm});
            skLineSegment(sketch, "E57.0.3.0", {"start": v(14, 25.3) * mm, "end": v(-14, 25.3) * mm});
            skLineSegment(sketch, "E57.0.3.1", {"start": v(-14, 23.3) * mm, "end": v(-14, 25.3) * mm});
            skLineSegment(sketch, "E57.0.3.2", {"start": v(14, 23.3) * mm, "end": v(-14, 23.3) * mm});
            skLineSegment(sketch, "E57.0.3.3", {"start": v(14, 23.3) * mm, "end": v(14, 25.3) * mm});
            skLineSegment(sketch, "E57.0.4.0", {"start": v(14, 19.3) * mm, "end": v(-14, 19.3) * mm});
            skLineSegment(sketch, "E57.0.4.1", {"start": v(-14, 17.3) * mm, "end": v(-14, 19.3) * mm});
            skLineSegment(sketch, "E57.0.4.2", {"start": v(14, 17.3) * mm, "end": v(-14, 17.3) * mm});
            skLineSegment(sketch, "E57.0.4.3", {"start": v(14, 17.3) * mm, "end": v(14, 19.3) * mm});
            skLineSegment(sketch, "E57.0.5.0", {"start": v(14, 13.3) * mm, "end": v(-14, 13.3) * mm});
            skLineSegment(sketch, "E57.0.5.1", {"start": v(-14, 11.3) * mm, "end": v(-14, 13.3) * mm});
            skLineSegment(sketch, "E57.0.5.2", {"start": v(14, 11.3) * mm, "end": v(-14, 11.3) * mm});
            skLineSegment(sketch, "E57.0.5.3", {"start": v(14, 11.3) * mm, "end": v(14, 13.3) * mm});
            skLineSegment(sketch, "E57.0.6.0", {"start": v(14, 7.3) * mm, "end": v(-14, 7.3) * mm});
            skLineSegment(sketch, "E57.0.6.1", {"start": v(-14, 5.3) * mm, "end": v(-14, 7.3) * mm});
            skLineSegment(sketch, "E57.0.6.2", {"start": v(14, 5.3) * mm, "end": v(-14, 5.3) * mm});
            skLineSegment(sketch, "E57.0.6.3", {"start": v(14, 5.3) * mm, "end": v(14, 7.3) * mm});
            skLineSegment(sketch, "E57.direction1", {"start": v(-14, 43.3) * mm, "end": v(11, 43.3) * mm, "construction": true});
            skLineSegment(sketch, "E57.direction2", {"start": v(-14, 43.3) * mm, "end": v(-14, 37.3) * mm, "construction": true});
            skSolve(sketch);
        }
        {
            var Q1;
            Q1=makeQuery(id+"F6.imprint","IMPRINT",FACE,{"disambiguationData":[TD([[makeQuery(id+"F6.imprint","IMPRINT",EDGE,{"derivedFrom":sQuery(id+"F6.wireOp",EDGE,"E52.bottom")}),-1.0]])]});
            var Q2;
            Q2=makeQuery(id+"F7.imprint","IMPRINT",FACE,{"disambiguationData":[TD([[makeQuery(id+"F7.imprint","IMPRINT",EDGE,{"derivedFrom":sQuery(id+"F7.wireOp",EDGE,"E56.bottom")}),-1.0]])]});
            loft(context, id + "F8", {"operationType" : NewBodyOperationType.REMOVE, "sheetProfilesArray" : [{ "sheetProfileEntities" : qUnion([Q1]) }, { "sheetProfileEntities" : qUnion([Q2]) }]});
        }
        {
            var Q1;
            Q1=makeQuery(id+"F6.imprint","IMPRINT",FACE,{"disambiguationData":[TD([[makeQuery(id+"F6.imprint","IMPRINT",EDGE,{"derivedFrom":sQuery(id+"F6.wireOp",EDGE,"E53.0.1.0")}),-1.0]])]});
            var Q2;
            Q2=makeQuery(id+"F7.imprint","IMPRINT",FACE,{"disambiguationData":[TD([[makeQuery(id+"F7.imprint","IMPRINT",EDGE,{"derivedFrom":sQuery(id+"F7.wireOp",EDGE,"E57.0.1.0")}),1.0]])]});
            loft(context, id + "F9", {"operationType" : NewBodyOperationType.REMOVE, "sheetProfilesArray" : [{ "sheetProfileEntities" : qUnion([Q1]) }, { "sheetProfileEntities" : qUnion([Q2]) }]});
        }
        {
            var Q1;
            Q1=makeQuery(id+"F6.imprint","IMPRINT",FACE,{"disambiguationData":[TD([[makeQuery(id+"F6.imprint","IMPRINT",EDGE,{"derivedFrom":sQuery(id+"F6.wireOp",EDGE,"E53.0.2.0")}),-1.0]])]});
            var Q2;
            Q2=makeQuery(id+"F7.imprint","IMPRINT",FACE,{"disambiguationData":[TD([[makeQuery(id+"F7.imprint","IMPRINT",EDGE,{"derivedFrom":sQuery(id+"F7.wireOp",EDGE,"E57.0.2.0")}),1.0]])]});
            loft(context, id + "F10", {"operationType" : NewBodyOperationType.REMOVE, "sheetProfilesArray" : [{ "sheetProfileEntities" : qUnion([Q1]) }, { "sheetProfileEntities" : qUnion([Q2]) }]});
        }
        {
            var Q1;
            Q1=makeQuery(id+"F6.imprint","IMPRINT",FACE,{"disambiguationData":[TD([[makeQuery(id+"F6.imprint","IMPRINT",EDGE,{"derivedFrom":sQuery(id+"F6.wireOp",EDGE,"E53.0.3.0")}),-1.0]])]});
            var Q2;
            Q2=makeQuery(id+"F7.imprint","IMPRINT",FACE,{"disambiguationData":[TD([[makeQuery(id+"F7.imprint","IMPRINT",EDGE,{"derivedFrom":sQuery(id+"F7.wireOp",EDGE,"E57.0.3.0")}),1.0]])]});
            loft(context, id + "F11", {"operationType" : NewBodyOperationType.REMOVE, "sheetProfilesArray" : [{ "sheetProfileEntities" : qUnion([Q1]) }, { "sheetProfileEntities" : qUnion([Q2]) }]});
        }
        {
            var Q1;
            Q1=makeQuery(id+"F7.imprint","IMPRINT",FACE,{"disambiguationData":[TD([[makeQuery(id+"F7.imprint","IMPRINT",EDGE,{"derivedFrom":sQuery(id+"F7.wireOp",EDGE,"E57.0.4.0")}),1.0]])]});
            var Q2;
            Q2=makeQuery(id+"F6.imprint","IMPRINT",FACE,{"disambiguationData":[TD([[makeQuery(id+"F6.imprint","IMPRINT",EDGE,{"derivedFrom":sQuery(id+"F6.wireOp",EDGE,"E53.0.4.0")}),-1.0]])]});
            loft(context, id + "F12", {"operationType" : NewBodyOperationType.REMOVE, "sheetProfilesArray" : [{ "sheetProfileEntities" : qUnion([Q1]) }, { "sheetProfileEntities" : qUnion([Q2]) }]});
        }
        {
            var Q1;
            Q1=makeQuery(id+"F7.imprint","IMPRINT",FACE,{"disambiguationData":[TD([[makeQuery(id+"F7.imprint","IMPRINT",EDGE,{"derivedFrom":sQuery(id+"F7.wireOp",EDGE,"E57.0.5.0")}),1.0]])]});
            var Q2;
            Q2=makeQuery(id+"F6.imprint","IMPRINT",FACE,{"disambiguationData":[TD([[makeQuery(id+"F6.imprint","IMPRINT",EDGE,{"derivedFrom":sQuery(id+"F6.wireOp",EDGE,"E53.0.5.0")}),-1.0]])]});
            loft(context, id + "F13", {"operationType" : NewBodyOperationType.REMOVE, "sheetProfilesArray" : [{ "sheetProfileEntities" : qUnion([Q1]) }, { "sheetProfileEntities" : qUnion([Q2]) }]});
        }
        {
            var Q1;
            Q1=makeQuery(id+"F7.imprint","IMPRINT",FACE,{"disambiguationData":[TD([[makeQuery(id+"F7.imprint","IMPRINT",EDGE,{"derivedFrom":sQuery(id+"F7.wireOp",EDGE,"E57.0.6.0")}),1.0]])]});
            var Q2;
            Q2=makeQuery(id+"F6.imprint","IMPRINT",FACE,{"disambiguationData":[TD([[makeQuery(id+"F6.imprint","IMPRINT",EDGE,{"derivedFrom":sQuery(id+"F6.wireOp",EDGE,"E54.0.0.6")}),-1.0]])]});
            loft(context, id + "F14", {"operationType" : NewBodyOperationType.REMOVE, "sheetProfilesArray" : [{ "sheetProfileEntities" : qUnion([Q1]) }, { "sheetProfileEntities" : qUnion([Q2]) }]});
        }
        {
            var Q0;
            Q0=makeQuery(id+"F4.imprint","IMPRINT",FACE,{"disambiguationData":[TD([[makeQuery(id+"F4.imprint","IMPRINT",EDGE,{"derivedFrom":sQuery(id+"F4.wireOp",EDGE,"E38.1.1.9")}),1.0]])]});
            var Q1;
            Q1=makeQuery(id+"F4.imprint","IMPRINT",FACE,{"disambiguationData":[TD([[makeQuery(id+"F4.imprint","IMPRINT",EDGE,{"derivedFrom":sQuery(id+"F4.wireOp",EDGE,"E38.0.1.9")}),1.0]])]});
            var Q2;
            Q2=makeQuery(id+"F4.imprint","IMPRINT",FACE,{"disambiguationData":[TD([[makeQuery(id+"F4.imprint","IMPRINT",EDGE,{"derivedFrom":sQuery(id+"F4.wireOp",EDGE,"E38.1.0.9")}),1.0]])]});
            var Q3;
            Q3=makeQuery(id+"F4.imprint","IMPRINT",FACE,{"disambiguationData":[TD([[makeQuery(id+"F4.imprint","IMPRINT",EDGE,{"derivedFrom":sQuery(id+"F4.wireOp",EDGE,"E35")}),-1.0]])]});
            var Q4;
            Q4=makeQuery(id+"F4.imprint","IMPRINT",FACE,{"disambiguationData":[TD([[makeQuery(id+"F4.imprint","IMPRINT",EDGE,{"derivedFrom":sQuery(id+"F4.wireOp",EDGE,"E39.0.1.28")}),-1.0]])]});
            var Q5;
            Q5=makeQuery(id+"F4.imprint","IMPRINT",FACE,{"disambiguationData":[TD([[makeQuery(id+"F4.imprint","IMPRINT",EDGE,{"derivedFrom":sQuery(id+"F4.wireOp",EDGE,"E39.0.1.26")}),1.0]])]});
            extrude(context, id + "F15", {"entities" : qUnion([Q0, Q1, Q2, Q3, Q4, Q5]), "operationType" : NewBodyOperationType.REMOVE, "endBound" : BoundingType.THROUGH_ALL, "oppositeDirection" : true, "depth" : 25 * mm});
        }
        {
            var Q0;
            Q0=makeQuery(id+"F1.opExtrude","SWEPT_FACE",FACE,{"disambiguationData":[OSD([sQuery(id+"F0.wireOp",EDGE,"E1"),sQuery(id+"F0.wireOp",EDGE,"E13.MirrorCS")])]});
            var sketch = newSketch(context, id + "F16", { "sketchPlane" : qUnion([Q0])});
            skCircle(sketch, "E58.0", {"center": v(12, 0) * mm, "radius": 3.85 * mm});
            skCircle(sketch, "E59.0", {"center": v(-12, 0) * mm, "radius": 3.85 * mm});
            skCircle(sketch, "E60.0", {"center": v(-12, -53) * mm, "radius": 3.85 * mm});
            skCircle(sketch, "E61.0", {"center": v(12, -53) * mm, "radius": 3.85 * mm});
            skCircle(sketch, "E62.0", {"center": v(-12, 53) * mm, "radius": 3.85 * mm});
            skCircle(sketch, "E63.0", {"center": v(12, 53) * mm, "radius": 3.85 * mm});
            skSolve(sketch);
        }
        {
            var Q0;
            Q0=makeQuery(id+"F2.opExtrude","CAP_FACE",FACE,{"disambiguationData":[OSD([sQuery(id+"F0.wireOp",EDGE,"E0"),sQuery(id+"F0.wireOp",EDGE,"E1"),sQuery(id+"F0.wireOp",EDGE,"E2"),sQuery(id+"F0.wireOp",EDGE,"E3"),sQuery(id+"F0.wireOp",EDGE,"E4"),sQuery(id+"F0.wireOp",EDGE,"E5"),sQuery(id+"F0.wireOp",EDGE,"E6.filletArc"),sQuery(id+"F0.wireOp",EDGE,"E7.MirrorCS"),sQuery(id+"F0.wireOp",EDGE,"E8.MirrorCS"),sQuery(id+"F0.wireOp",EDGE,"E9.MirrorCS"),sQuery(id+"F0.wireOp",EDGE,"E10.MirrorCS"),sQuery(id+"F0.wireOp",EDGE,"E11.MirrorCS"),sQuery(id+"F0.wireOp",EDGE,"E12.MirrorCS"),sQuery(id+"F0.wireOp",EDGE,"E13.MirrorCS"),sQuery(id+"F0.wireOp",EDGE,"E15.MirrorCS"),sQuery(id+"F0.wireOp",EDGE,"E23")])],"isStart":false});
            var sketch = newSketch(context, id + "F17", { "sketchPlane" : qUnion([Q0])});
            skLineSegment(sketch, "E64.bottom", {"start": v(16.9, 19) * mm, "end": v(-16.9, 19) * mm});
            skLineSegment(sketch, "E64.top", {"start": v(16.9, -19) * mm, "end": v(-16.9, -19) * mm});
            skLineSegment(sketch, "E64.left", {"start": v(19.4, 16.5) * mm, "end": v(19.4, -16.5) * mm});
            skLineSegment(sketch, "E64.right", {"start": v(-19.4, 16.5) * mm, "end": v(-19.4, -16.5) * mm});
            skPoint(sketch, "E64.middle", {"position": v(0, 0) * mm});
            skCircle(sketch, "E65", {"center": v(0, 0) * mm, "radius": 3 * mm});
            skPoint(sketch, "E66.visualSharp", {"position": v(-19.4, 19) * mm});
            skArc(sketch, "E66.filletArc", {"start": v(-16.9, 19) * mm, "mid": v(-18.67, 18.27) * mm, "end": v(-19.4, 16.5) * mm});
            skPoint(sketch, "E67.visualSharp", {"position": v(19.4, 19) * mm});
            skArc(sketch, "E67.filletArc", {"start": v(19.4, 16.5) * mm, "mid": v(18.67, 18.27) * mm, "end": v(16.9, 19) * mm});
            skPoint(sketch, "E68.visualSharp", {"position": v(19.4, -19) * mm});
            skArc(sketch, "E68.filletArc", {"start": v(16.9, -19) * mm, "mid": v(18.67, -18.27) * mm, "end": v(19.4, -16.5) * mm});
            skPoint(sketch, "E69.visualSharp", {"position": v(-19.4, -19) * mm});
            skArc(sketch, "E69.filletArc", {"start": v(-19.4, -16.5) * mm, "mid": v(-18.67, -18.27) * mm, "end": v(-16.9, -19) * mm});
            skSolve(sketch);
        }
        {
            var Q0;
            Q0=makeQuery(id+"F17.imprint","IMPRINT",FACE,{"disambiguationData":[TD([[makeQuery(id+"F17.imprint","IMPRINT",EDGE,{"derivedFrom":sQuery(id+"F17.wireOp",EDGE,"E64.top")}),-1.0]])]});
            var Q1;
            Q1=makeQuery(id+"F17.imprint","IMPRINT",FACE,{"disambiguationData":[TD([[makeQuery(id+"F17.imprint","IMPRINT",EDGE,{"derivedFrom":sQuery(id+"F17.wireOp",EDGE,"E64.bottom")}),1.0]])]});
            var Q2;
            Q2=makeQuery(id+"F17.imprint","IMPRINT",FACE,{"disambiguationData":[TD([[makeQuery(id+"F17.imprint","IMPRINT",EDGE,{"derivedFrom":sQuery(id+"F17.wireOp",EDGE,"E65")}),-1.0]])]});
            var Q3;
            Q3=makeQuery(id+"F17.imprint","IMPRINT",FACE,{"disambiguationData":[TD([[makeQuery(id+"F17.imprint","IMPRINT",EDGE,{"derivedFrom":sQuery(id+"F17.wireOp",EDGE,"nD8Kwe0E-LyN5-9v3S-HhZ5-6PXcykFEMyGh")}),-1.0]])]});
            var Q4;
            {var subQ0=sQuery(id+"F17.wireOp",EDGE,"8OaGibdO-s63X-WpAR-fF8m-tR8zLJGH6z30.bottom");Q4=makeQuery(id+"F17.imprint","IMPRINT",FACE,{"disambiguationData":[TD([[makeQuery(id+"F17.imprint","IMPRINT",EDGE,{"derivedFrom":subQ0}),1.0]])]});}
            var Q5;
            {var subQ0=sQuery(id+"F17.wireOp",EDGE,"2b9ee071-3f00-4acf-bb48-5342cdfde70b0.MirrorCS");Q5=makeQuery(id+"F17.imprint","IMPRINT",FACE,{"disambiguationData":[TD([[makeQuery(id+"F17.imprint","IMPRINT",EDGE,{"derivedFrom":subQ0}),-1.0]])]});}
            var Q6;
            {var subQ0=sQuery(id+"F17.wireOp",EDGE,"f665b046-b4de-4646-a277-42cbfe046c250.MirrorCS");Q6=makeQuery(id+"F17.imprint","IMPRINT",FACE,{"disambiguationData":[TD([[makeQuery(id+"F17.imprint","IMPRINT",EDGE,{"derivedFrom":subQ0}),1.0]])]});}
            var Q7;
            {var subQ0=sQuery(id+"F17.wireOp",EDGE,"8OaGibdO-s63X-WpAR-fF8m-tR8zLJGH6z30.left");Q7=makeQuery(id+"F17.imprint","IMPRINT",FACE,{"disambiguationData":[TD([[makeQuery(id+"F17.imprint","IMPRINT",EDGE,{"derivedFrom":subQ0}),-1.0]])]});}
            var Q8;
            {var subQ6=sQuery(id+"F17.wireOp",EDGE,"f665b046-b4de-4646-a277-42cbfe046c250.MirrorCS");Q8=makeQuery(id+"F17.imprint","IMPRINT",FACE,{"disambiguationData":[TD([[makeQuery(id+"F17.imprint","IMPRINT",EDGE,{"derivedFrom":subQ6}),-1.0]])]});}
            var Q9;
            {var subQ7=sQuery(id+"F17.wireOp",EDGE,"jx2pznYv-WiQa-t24E-UubQ-obQmXljIExVI");Q9=makeQuery(id+"F17.imprint","IMPRINT",FACE,{"disambiguationData":[TD([[makeQuery(id+"F17.imprint","IMPRINT",EDGE,{"derivedFrom":subQ7}),1.0]])]});}
            var Q10;
            {var subQ0=sQuery(id+"F17.wireOp",EDGE,"Tgq0GRvB-8IHy-bL1C-Ft6y-5T5eVKgj73xW");var subQ1=sQuery(id+"F17.wireOp",EDGE,"w3musNCA-F7QQ-4Qe7-eHCE-RSl8asJhhDmV");var subQ2=makeQuery(id+"F17.imprint","INTERSECT",VERTEX,{"derivedFrom":[subQ1,subQ0]});Q10=makeQuery(id+"F17.imprint","IMPRINT",FACE,{"disambiguationData":[TD([[makeQuery(id+"F17.imprint","IMPRINT",EDGE,{"disambiguationData":[TD([[subQ2,-1.0]])],"derivedFrom":subQ1}),1.0]])]});}
            var Q11;
            {var subQ7=sQuery(id+"F17.wireOp",EDGE,"f2c99bd5-d463-4452-8829-1bb3593946590.MirrorCS");Q11=makeQuery(id+"F17.imprint","IMPRINT",FACE,{"disambiguationData":[TD([[makeQuery(id+"F17.imprint","IMPRINT",EDGE,{"derivedFrom":subQ7}),-1.0]])]});}
            var Q12;
            {var subQ0=sQuery(id+"F17.wireOp",EDGE,"b3e39073-35ed-4b7e-9a34-1a8f38f34e3c0.MirrorCS");Q12=makeQuery(id+"F17.imprint","IMPRINT",FACE,{"disambiguationData":[TD([[makeQuery(id+"F17.imprint","IMPRINT",EDGE,{"derivedFrom":subQ0}),1.0]])]});}
            var Q13;
            {var subQ1=sQuery(id+"F17.wireOp",EDGE,"w3musNCA-F7QQ-4Qe7-eHCE-RSl8asJhhDmV");var subQ3=sQuery(id+"F17.wireOp",EDGE,"a4bf64f6-2d18-40c4-9ec0-d416768209660.MirrorCS");var subQ4=makeQuery(id+"F17.imprint","INTERSECT",VERTEX,{"derivedFrom":[subQ1,subQ3]});Q13=makeQuery(id+"F17.imprint","IMPRINT",FACE,{"disambiguationData":[TD([[makeQuery(id+"F17.imprint","IMPRINT",EDGE,{"disambiguationData":[TD([[subQ4,-1.0]])],"derivedFrom":subQ3}),-1.0]])]});}
            var Q14;
            {var subQ0=sQuery(id+"F17.wireOp",EDGE,"a4bf64f6-2d18-40c4-9ec0-d416768209660.MirrorCS");var subQ1=sQuery(id+"F17.wireOp",EDGE,"w3musNCA-F7QQ-4Qe7-eHCE-RSl8asJhhDmV");var subQ2=makeQuery(id+"F17.imprint","INTERSECT",VERTEX,{"derivedFrom":[subQ1,subQ0]});Q14=makeQuery(id+"F17.imprint","IMPRINT",FACE,{"disambiguationData":[TD([[makeQuery(id+"F17.imprint","IMPRINT",EDGE,{"disambiguationData":[TD([[subQ2,1.0]])],"derivedFrom":subQ1}),1.0]])]});}
            var Q15;
            {var subQ7=sQuery(id+"F17.wireOp",EDGE,"xZBimn0j-09uR-lKZF-jL7g-mSEd3W3b6ZDA");Q15=makeQuery(id+"F17.imprint","IMPRINT",FACE,{"disambiguationData":[TD([[makeQuery(id+"F17.imprint","IMPRINT",EDGE,{"derivedFrom":subQ7}),-1.0]])]});}
            var Q16;
            {var subQ3=sQuery(id+"F17.wireOp",EDGE,"3f8a3118-b42e-4bc8-bdd2-8b6aaac7346e0.MirrorCS");Q16=makeQuery(id+"F17.imprint","IMPRINT",FACE,{"disambiguationData":[TD([[makeQuery(id+"F17.imprint","IMPRINT",EDGE,{"derivedFrom":subQ3}),-1.0]])]});}
            var Q17;
            {var subQ1=sQuery(id+"F17.wireOp",EDGE,"w3musNCA-F7QQ-4Qe7-eHCE-RSl8asJhhDmV");var subQ3=sQuery(id+"F17.wireOp",EDGE,"Tgq0GRvB-8IHy-bL1C-Ft6y-5T5eVKgj73xW");var subQ4=makeQuery(id+"F17.imprint","INTERSECT",VERTEX,{"derivedFrom":[subQ1,subQ3]});Q17=makeQuery(id+"F17.imprint","IMPRINT",FACE,{"disambiguationData":[TD([[makeQuery(id+"F17.imprint","IMPRINT",EDGE,{"disambiguationData":[TD([[subQ4,-1.0]])],"derivedFrom":subQ3}),1.0]])]});}
            extrude(context, id + "F18", {"entities" : qUnion([Q0, Q1, Q2, Q3, Q4, Q5, Q6, Q7, Q8, Q9, Q10, Q11, Q12, Q13, Q14, Q15, Q16, Q17]), "depth" : 2.5 * mm});
        }
        {
            var Q0;
            Q0=makeQuery(id+"F18.opExtrude","CAP_EDGE",EDGE,{"disambiguationData":[OSD([sQuery(id+"F17.wireOp",EDGE,"E64.bottom")])],"isStart":false});
            chamfer(context, id + "F19", {"entities" : qUnion([Q0]), "width" : 1.5 * mm, "tangentPropagation" : true});
        }
        {
            var Q0;
            Q0=makeQuery(id+"F17.imprint","IMPRINT",FACE,{"disambiguationData":[TD([[makeQuery(id+"F17.imprint","IMPRINT",EDGE,{"derivedFrom":sQuery(id+"F17.wireOp",EDGE,"E64.top")}),-1.0]])]});
            var sketch = newSketch(context, id + "F20", { "sketchPlane" : qUnion([Q0])});
            skLineSegment(sketch, "E70.bottom", {"start": v(16.9, 19) * mm, "end": v(-16.9, 19) * mm});
            skLineSegment(sketch, "E70.top", {"start": v(16.9, -19) * mm, "end": v(-16.9, -19) * mm});
            skLineSegment(sketch, "E70.left", {"start": v(19.4, 16.5) * mm, "end": v(19.4, -16.5) * mm});
            skLineSegment(sketch, "E70.right", {"start": v(-19.4, 16.5) * mm, "end": v(-19.4, -16.5) * mm});
            skPoint(sketch, "E70.middle", {"position": v(0, 0) * mm});
            skCircle(sketch, "E71", {"center": v(0, 0) * mm, "radius": 4 * mm});
            skCircle(sketch, "E72", {"center": v(0, 0) * mm, "radius": 7.25 * mm});
            skPoint(sketch, "E73.visualSharp", {"position": v(-19.4, 19) * mm});
            skArc(sketch, "E73.filletArc", {"start": v(-16.9, 19) * mm, "mid": v(-18.67, 18.27) * mm, "end": v(-19.4, 16.5) * mm});
            skPoint(sketch, "E74.visualSharp", {"position": v(19.4, 19) * mm});
            skArc(sketch, "E74.filletArc", {"start": v(19.4, 16.5) * mm, "mid": v(18.67, 18.27) * mm, "end": v(16.9, 19) * mm});
            skPoint(sketch, "E75.visualSharp", {"position": v(19.4, -19) * mm});
            skArc(sketch, "E75.filletArc", {"start": v(16.9, -19) * mm, "mid": v(18.67, -18.27) * mm, "end": v(19.4, -16.5) * mm});
            skPoint(sketch, "E76.visualSharp", {"position": v(-19.4, -19) * mm});
            skArc(sketch, "E76.filletArc", {"start": v(-19.4, -16.5) * mm, "mid": v(-18.67, -18.27) * mm, "end": v(-16.9, -19) * mm});
            skCircle(sketch, "E77", {"center": v(0, 0) * mm, "radius": 9.25 * mm});
            skLineSegment(sketch, "E78", {"start": v(7.44, -5.5) * mm, "end": v(15.2, -5.5) * mm});
            skLineSegment(sketch, "E79", {"start": v(15.2, -5.5) * mm, "end": v(15.2, 5.47) * mm});
            skLineSegment(sketch, "E80", {"start": v(15.2, 5.47) * mm, "end": v(7.46, 5.47) * mm});
            skLineSegment(sketch, "E81.MirrorCS", {"start": v(-15.2, 5.47) * mm, "end": v(-7.46, 5.47) * mm});
            skLineSegment(sketch, "E82.MirrorCS", {"start": v(-15.2, -5.5) * mm, "end": v(-15.2, 5.47) * mm});
            skLineSegment(sketch, "E83.MirrorCS", {"start": v(-7.44, -5.5) * mm, "end": v(-15.2, -5.5) * mm});
            skLineSegment(sketch, "E84", {"start": v(7.46, 5.47) * mm, "end": v(7.44, -5.5) * mm});
            skLineSegment(sketch, "E85", {"start": v(-7.46, 5.47) * mm, "end": v(-7.44, -5.5) * mm});
            skCircle(sketch, "E86", {"center": v(0, 0) * mm, "radius": 5.75 * mm});
            skSolve(sketch);
        }
        {
            var Q0;
            {var subQ0=makeQuery(id+"F17.imprint","IMPRINT",EDGE,{"derivedFrom":sQuery(id+"F17.wireOp",EDGE,"3f8a3118-b42e-4bc8-bdd2-8b6aaac7346e0.MirrorCS")});Q0=makeQuery(id+"F20.imprint","IMPRINT",FACE,{"disambiguationData":[TD([[makeQuery(id+"F20.imprint","IMPRINT",EDGE,{"derivedFrom":subQ0}),-1.0]])]});}
            var Q1;
            {var subQ2=sQuery(id+"F20.wireOp",EDGE,"E84");Q1=makeQuery(id+"F20.imprint","IMPRINT",FACE,{"disambiguationData":[TD([[makeQuery(id+"F20.imprint","IMPRINT",EDGE,{"derivedFrom":subQ2}),1.0]])]});}
            var Q2;
            {var subQ0=makeQuery(id+"F17.imprint","IMPRINT",EDGE,{"derivedFrom":sQuery(id+"F17.wireOp",EDGE,"8OaGibdO-s63X-WpAR-fF8m-tR8zLJGH6z30.bottom")});Q2=makeQuery(id+"F20.imprint","IMPRINT",FACE,{"disambiguationData":[TD([[makeQuery(id+"F20.imprint","IMPRINT",EDGE,{"derivedFrom":subQ0}),1.0]])]});}
            var Q3;
            {var subQ2=sQuery(id+"F20.wireOp",EDGE,"E85");Q3=makeQuery(id+"F20.imprint","IMPRINT",FACE,{"disambiguationData":[TD([[makeQuery(id+"F20.imprint","IMPRINT",EDGE,{"derivedFrom":subQ2}),-1.0]])]});}
            var Q4;
            {var subQ2=sQuery(id+"F20.wireOp",EDGE,"E81.MirrorCS");Q4=makeQuery(id+"F20.imprint","IMPRINT",FACE,{"disambiguationData":[TD([[makeQuery(id+"F20.imprint","IMPRINT",EDGE,{"derivedFrom":subQ2}),-1.0]])]});}
            var Q5;
            {var subQ2=sQuery(id+"F20.wireOp",EDGE,"E80");Q5=makeQuery(id+"F20.imprint","IMPRINT",FACE,{"disambiguationData":[TD([[makeQuery(id+"F20.imprint","IMPRINT",EDGE,{"derivedFrom":subQ2}),1.0]])]});}
            var Q6;
            Q6=makeQuery(id+"F20.imprint","IMPRINT",FACE,{"disambiguationData":[TD([[makeQuery(id+"F20.imprint","IMPRINT",EDGE,{"derivedFrom":sQuery(id+"F20.wireOp",EDGE,"E72")}),-1.0]])]});
            var Q7;
            {var subQ1=sQuery(id+"F17.wireOp",EDGE,"830ca9db-2278-4f42-afff-de19992612cc0.MirrorCS");var subQ2=makeQuery(id+"F17.imprint","IMPRINT",EDGE,{"disambiguationData":[TD([[makeQuery(id+"F17.imprint","INTERSECT",VERTEX,{"derivedFrom":[sQuery(id+"F17.wireOp",EDGE,"5009a031-9101-433e-b9ca-c077b01db3660.MirrorCS"),subQ1]}),-1.0]])],"derivedFrom":subQ1});Q7=makeQuery(id+"F20.imprint","IMPRINT",FACE,{"disambiguationData":[TD([[makeQuery(id+"F20.imprint","IMPRINT",EDGE,{"derivedFrom":subQ2}),1.0]])]});}
            var Q8;
            {var subQ1=sQuery(id+"F17.wireOp",EDGE,"lKL4IWFX-4cPn-TcOg-gEkC-57tgTnEDoaRi");var subQ2=makeQuery(id+"F17.imprint","IMPRINT",EDGE,{"disambiguationData":[TD([[makeQuery(id+"F17.imprint","INTERSECT",VERTEX,{"derivedFrom":[sQuery(id+"F17.wireOp",EDGE,"m03xCCtB-JWrN-DkoU-RA7p-SOQiGAv66X5g"),subQ1]}),-1.0]])],"derivedFrom":subQ1});Q8=makeQuery(id+"F20.imprint","IMPRINT",FACE,{"disambiguationData":[TD([[makeQuery(id+"F20.imprint","IMPRINT",EDGE,{"derivedFrom":subQ2}),-1.0]])]});}
            var Q9;
            Q9=makeQuery(id+"F5.opExtrude","SWEPT_FACE",FACE,{"disambiguationData":[OSD([sQuery(id+"F4.wireOp",EDGE,"E39.0.1.11"),sQuery(id+"F4.wireOp",EDGE,"E39.0.1.22")])]});
            extrude(context, id + "F21", {"entities" : qUnion([Q0, Q1, Q2, Q3, Q4, Q5, Q6, Q7, Q8]), "operationType" : NewBodyOperationType.ADD, "oppositeDirection" : true, "endBoundEntityFace" : qUnion([Q9]), "depth" : 12 * mm});
        }
        {
            var Q0;
            Q0=makeQuery(id+"F20.imprint","IMPRINT",FACE,{"disambiguationData":[TD([[makeQuery(id+"F20.imprint","IMPRINT",EDGE,{"derivedFrom":sQuery(id+"F20.wireOp",EDGE,"E72")}),1.0]])]});
            extrude(context, id + "F22", {"entities" : qUnion([Q0]), "operationType" : NewBodyOperationType.ADD, "oppositeDirection" : true, "depth" : 7 * mm});
        }
        {
            var Q0;
            Q0=makeQuery(id+"F21.opExtrude","SWEPT_FACE",FACE,{"disambiguationData":[OSD([sQuery(id+"F20.wireOp",EDGE,"E80")])]});
            var sketch = newSketch(context, id + "F23", { "sketchPlane" : qUnion([Q0])});
            skLineSegment(sketch, "E87", {"start": v(12, -53) * mm, "end": v(12, -52) * mm});
            skLineSegment(sketch, "E88", {"start": v(12, -53) * mm, "end": v(12, -54) * mm});
            skArc(sketch, "E89.0.startCap", {"start": v(13.4, -53) * mm, "mid": v(12, -54.4) * mm, "end": v(10.6, -53) * mm});
            skArc(sketch, "E89.0.endCap", {"start": v(10.6, -52) * mm, "mid": v(12, -50.6) * mm, "end": v(13.4, -52) * mm});
            skLineSegment(sketch, "E89.0.left", {"start": v(10.6, -53) * mm, "end": v(10.6, -52) * mm});
            skLineSegment(sketch, "E89.0.right", {"start": v(13.4, -53) * mm, "end": v(13.4, -52) * mm});
            skArc(sketch, "E89.1.startCap", {"start": v(10.6, -53) * mm, "mid": v(12, -51.6) * mm, "end": v(13.4, -53) * mm});
            skArc(sketch, "E89.1.endCap", {"start": v(13.4, -54) * mm, "mid": v(12, -55.4) * mm, "end": v(10.6, -54) * mm});
            skLineSegment(sketch, "E89.1.left", {"start": v(13.4, -53) * mm, "end": v(13.4, -54) * mm});
            skLineSegment(sketch, "E89.1.right", {"start": v(10.6, -53) * mm, "end": v(10.6, -54) * mm});
            skLineSegment(sketch, "E90.MirrorCS", {"start": v(-13.4, -53) * mm, "end": v(-13.4, -52) * mm});
            skArc(sketch, "E91.MirrorCS", {"start": v(-10.6, -53) * mm, "mid": v(-12, -51.6) * mm, "end": v(-13.4, -53) * mm});
            skLineSegment(sketch, "E92.MirrorCS", {"start": v(-10.6, -53) * mm, "end": v(-10.6, -52) * mm});
            skArc(sketch, "E93.MirrorCS", {"start": v(-10.6, -52) * mm, "mid": v(-12, -50.6) * mm, "end": v(-13.4, -52) * mm});
            skArc(sketch, "E94.MirrorCS", {"start": v(-13.4, -53) * mm, "mid": v(-12, -54.4) * mm, "end": v(-10.6, -53) * mm});
            skLineSegment(sketch, "E95.MirrorCS", {"start": v(-12, -53) * mm, "end": v(-12, -52) * mm});
            skLineSegment(sketch, "E96.MirrorCS", {"start": v(-12, -53) * mm, "end": v(-12, -54) * mm});
            skArc(sketch, "E97.MirrorCS", {"start": v(-13.4, -54) * mm, "mid": v(-12, -55.4) * mm, "end": v(-10.6, -54) * mm});
            skLineSegment(sketch, "E98.MirrorCS", {"start": v(-10.6, -53) * mm, "end": v(-10.6, -54) * mm});
            skLineSegment(sketch, "E99.MirrorCS", {"start": v(-13.4, -53) * mm, "end": v(-13.4, -54) * mm});
            skSolve(sketch);
        }
        {
            var Q0;
            Q0=makeQuery(id+"F23.imprint","IMPRINT",FACE,{"disambiguationData":[TD([[makeQuery(id+"F23.imprint","IMPRINT",EDGE,{"derivedFrom":sQuery(id+"F23.wireOp",EDGE,"E89.0.endCap")}),-1.0]])]});
            var Q1;
            Q1=makeQuery(id+"F23.imprint","IMPRINT",FACE,{"disambiguationData":[TD([[makeQuery(id+"F23.imprint","IMPRINT",EDGE,{"derivedFrom":sQuery(id+"F23.wireOp",EDGE,"E89.0.startCap")}),-1.0]])]});
            var Q2;
            Q2=makeQuery(id+"F23.imprint","IMPRINT",FACE,{"disambiguationData":[TD([[makeQuery(id+"F23.imprint","IMPRINT",EDGE,{"derivedFrom":sQuery(id+"F23.wireOp",EDGE,"E89.0.startCap")}),1.0]])]});
            var Q3;
            Q3=makeQuery(id+"F23.imprint","IMPRINT",FACE,{"disambiguationData":[TD([[makeQuery(id+"F23.imprint","IMPRINT",EDGE,{"derivedFrom":sQuery(id+"F23.wireOp",EDGE,"E90.MirrorCS")}),-1.0]])]});
            var Q4;
            Q4=makeQuery(id+"F23.imprint","IMPRINT",FACE,{"disambiguationData":[TD([[makeQuery(id+"F23.imprint","IMPRINT",EDGE,{"derivedFrom":sQuery(id+"F23.wireOp",EDGE,"E91.MirrorCS")}),1.0]])]});
            var Q5;
            Q5=makeQuery(id+"F23.imprint","IMPRINT",FACE,{"disambiguationData":[TD([[makeQuery(id+"F23.imprint","IMPRINT",EDGE,{"derivedFrom":sQuery(id+"F23.wireOp",EDGE,"E94.MirrorCS")}),-1.0]])]});
            extrude(context, id + "F24", {"entities" : qUnion([Q0, Q1, Q2, Q3, Q4, Q5]), "operationType" : NewBodyOperationType.REMOVE, "endBound" : BoundingType.UP_TO_NEXT, "oppositeDirection" : true, "depth" : 25 * mm});
        }
        {
            var Q0;
            Q0=makeQuery(id+"F2.opExtrude","SWEPT_FACE",FACE,{"disambiguationData":[OSD([sQuery(id+"F0.wireOp",EDGE,"E28")])]});
            var sketch = newSketch(context, id + "F25", { "sketchPlane" : qUnion([Q0])});
            skLineSegment(sketch, "E100.bottom", {"start": v(-15.4, 2.7) * mm, "end": v(-8.59, 2.7) * mm});
            skLineSegment(sketch, "E100.top", {"start": v(-15.4, -2.7) * mm, "end": v(-8.59, -2.7) * mm});
            skLineSegment(sketch, "E100.left", {"start": v(-15.4, 2.7) * mm, "end": v(-15.4, -2.7) * mm});
            skLineSegment(sketch, "E100.right", {"start": v(-8.59, 2.7) * mm, "end": v(-8.59, -2.7) * mm});
            skPoint(sketch, "E100.middle", {"position": v(-12, 0) * mm});
            skCircle(sketch, "E101", {"center": v(-12, 0) * mm, "radius": 1.4 * mm});
            skLineSegment(sketch, "E102.0.1.0", {"start": v(-15.4, 50.3) * mm, "end": v(-8.59, 50.3) * mm});
            skPoint(sketch, "E102.0.1.1", {"position": v(-12, 53) * mm});
            skLineSegment(sketch, "E102.0.1.2", {"start": v(-15.4, 55.7) * mm, "end": v(-8.59, 55.7) * mm});
            skLineSegment(sketch, "E102.0.1.3", {"start": v(-15.4, 55.7) * mm, "end": v(-15.4, 50.3) * mm});
            skLineSegment(sketch, "E102.0.1.4", {"start": v(-8.59, 55.7) * mm, "end": v(-8.59, 50.3) * mm});
            skCircle(sketch, "E102.0.1.5", {"center": v(-12, 53) * mm, "radius": 1.4 * mm});
            skLineSegment(sketch, "E102.1.0.0", {"start": v(8.6, -2.7) * mm, "end": v(15.41, -2.7) * mm});
            skPoint(sketch, "E102.1.0.1", {"position": v(12, 0) * mm});
            skLineSegment(sketch, "E102.1.0.2", {"start": v(8.6, 2.7) * mm, "end": v(15.41, 2.7) * mm});
            skLineSegment(sketch, "E102.1.0.3", {"start": v(8.6, 2.7) * mm, "end": v(8.6, -2.7) * mm});
            skLineSegment(sketch, "E102.1.0.4", {"start": v(15.41, 2.7) * mm, "end": v(15.41, -2.7) * mm});
            skCircle(sketch, "E102.1.0.5", {"center": v(12, 0) * mm, "radius": 1.4 * mm});
            skLineSegment(sketch, "E102.1.1.0", {"start": v(8.6, 50.3) * mm, "end": v(15.41, 50.3) * mm});
            skPoint(sketch, "E102.1.1.1", {"position": v(12, 53) * mm});
            skLineSegment(sketch, "E102.1.1.2", {"start": v(8.6, 55.7) * mm, "end": v(15.41, 55.7) * mm});
            skLineSegment(sketch, "E102.1.1.3", {"start": v(8.6, 55.7) * mm, "end": v(8.6, 50.3) * mm});
            skLineSegment(sketch, "E102.1.1.4", {"start": v(15.41, 55.7) * mm, "end": v(15.41, 50.3) * mm});
            skCircle(sketch, "E102.1.1.5", {"center": v(12, 53) * mm, "radius": 1.4 * mm});
            skLineSegment(sketch, "E102.direction1", {"start": v(-15.4, -2.7) * mm, "end": v(8.6, -2.7) * mm, "construction": true});
            skLineSegment(sketch, "E102.direction2", {"start": v(-15.4, -2.7) * mm, "end": v(-15.4, 50.3) * mm, "construction": true});
            skLineSegment(sketch, "E103", {"start": v(-15.4, -26.5) * mm, "end": v(15.4, -26.5) * mm, "construction": true});
            skCircle(sketch, "E104.MirrorC", {"center": v(-12, -53) * mm, "radius": 1.4 * mm});
            skCircle(sketch, "E105.MirrorC", {"center": v(12, -53) * mm, "radius": 1.4 * mm});
            skLineSegment(sketch, "E106.MirrorCS", {"start": v(-15.4, -50.3) * mm, "end": v(-8.59, -50.3) * mm});
            skLineSegment(sketch, "E107.MirrorCS", {"start": v(-8.59, -55.7) * mm, "end": v(-8.59, -50.3) * mm});
            skLineSegment(sketch, "E108.MirrorCS", {"start": v(-15.4, -55.7) * mm, "end": v(-8.59, -55.7) * mm});
            skLineSegment(sketch, "E109.MirrorCS", {"start": v(8.6, -50.3) * mm, "end": v(15.41, -50.3) * mm});
            skLineSegment(sketch, "E110.MirrorCS", {"start": v(8.6, -55.7) * mm, "end": v(15.41, -55.7) * mm});
            skLineSegment(sketch, "E111.MirrorCS", {"start": v(8.6, -55.7) * mm, "end": v(8.6, -50.3) * mm});
            skLineSegment(sketch, "E112.MirrorCS", {"start": v(15.41, -55.7) * mm, "end": v(15.41, -50.3) * mm});
            skLineSegment(sketch, "E113.MirrorCS", {"start": v(-15.4, -55.7) * mm, "end": v(-15.4, -50.3) * mm});
            skLineSegment(sketch, "E114.MirrorCS", {"start": v(-15.4, -50.3) * mm, "end": v(8.6, -50.3) * mm, "construction": true});
            skSolve(sketch);
        }
        {
            var Q0;
            Q0=makeQuery(id+"F25.imprint","IMPRINT",FACE,{"disambiguationData":[TD([[makeQuery(id+"F25.imprint","IMPRINT",EDGE,{"derivedFrom":sQuery(id+"F25.wireOp",EDGE,"E105.MirrorC")}),1.0]])]});
            var Q1;
            Q1=makeQuery(id+"F25.imprint","IMPRINT",FACE,{"disambiguationData":[TD([[makeQuery(id+"F25.imprint","IMPRINT",EDGE,{"derivedFrom":sQuery(id+"F25.wireOp",EDGE,"E104.MirrorC")}),1.0]])]});
            var Q2;
            {var subQ0=sQuery(id+"F25.wireOp",EDGE,"E102.1.0.3");Q2=makeQuery(id+"F25.imprint","IMPRINT",FACE,{"disambiguationData":[TD([[makeQuery(id+"F25.imprint","IMPRINT",EDGE,{"derivedFrom":subQ0}),1.0]])]});}
            var Q3;
            Q3=makeQuery(id+"F25.imprint","IMPRINT",FACE,{"disambiguationData":[TD([[makeQuery(id+"F25.imprint","IMPRINT",EDGE,{"derivedFrom":sQuery(id+"F25.wireOp",EDGE,"E100.bottom")}),-1.0]])]});
            var Q4;
            Q4=makeQuery(id+"F25.imprint","IMPRINT",FACE,{"disambiguationData":[TD([[makeQuery(id+"F25.imprint","IMPRINT",EDGE,{"derivedFrom":sQuery(id+"F25.wireOp",EDGE,"E102.0.1.0")}),1.0]])]});
            var Q5;
            {var subQ0=sQuery(id+"F25.wireOp",EDGE,"E102.1.1.3");Q5=makeQuery(id+"F25.imprint","IMPRINT",FACE,{"disambiguationData":[TD([[makeQuery(id+"F25.imprint","IMPRINT",EDGE,{"derivedFrom":subQ0}),1.0]])]});}
            extrude(context, id + "F26", {"entities" : qUnion([Q0, Q1, Q2, Q3, Q4, Q5]), "operationType" : NewBodyOperationType.ADD, "depth" : 10 * mm});
        }
        {
            var Q0;
            Q0=makeQuery(id+"F5.opExtrude","SWEPT_FACE",FACE,{"disambiguationData":[OSD([sQuery(id+"F4.wireOp",EDGE,"E43.top")])]});
            cPlane(context, id + "F27", {"entities" : qUnion([Q0]), "cplaneType" : CPlaneType.OFFSET, "offset" : 20 * mm, "oppositeDirection" : true, "width" : 150 * mm, "height" : 150 * mm});
        }
        {
            var Q0;
            Q0=qCreatedBy(id+"F27.planeOp",FACE);
            var sketch = newSketch(context, id + "F28", { "sketchPlane" : qUnion([Q0])});
            skLineSegment(sketch, "E115", {"start": v(-15.2, 5.5) * mm, "end": v(-15.2, -5.5) * mm});
            skCircle(sketch, "E116", {"center": v(0, 0) * mm, "radius": 7.15 * mm});
            skCircle(sketch, "E117.0", {"center": v(0, 0) * mm, "radius": 9.15 * mm});
            skLineSegment(sketch, "E118", {"start": v(-15.2, 5.5) * mm, "end": v(-7.31, 5.5) * mm});
            skLineSegment(sketch, "E119", {"start": v(-15.2, -5.5) * mm, "end": v(-7.31, -5.5) * mm});
            skLineSegment(sketch, "E120", {"start": v(-7.31, 5.5) * mm, "end": v(-7.31, -5.5) * mm});
            skLineSegment(sketch, "E121.MirrorCS", {"start": v(7.31, 5.5) * mm, "end": v(7.31, -5.5) * mm});
            skLineSegment(sketch, "E122.MirrorCS", {"start": v(15.2, -5.5) * mm, "end": v(7.31, -5.5) * mm});
            skLineSegment(sketch, "E123.MirrorCS", {"start": v(15.2, 5.5) * mm, "end": v(15.2, -5.5) * mm});
            skLineSegment(sketch, "E124.MirrorCS", {"start": v(15.2, 5.5) * mm, "end": v(7.31, 5.5) * mm});
            skSolve(sketch);
        }
        {
            var Q0;
            Q0=makeQuery(id+"F28.imprint","IMPRINT",FACE,{"disambiguationData":[TD([[makeQuery(id+"F28.imprint","IMPRINT",EDGE,{"derivedFrom":sQuery(id+"F28.wireOp",EDGE,"E115")}),1.0]])]});
            var Q1;
            {var subQ0=sQuery(id+"F28.wireOp",EDGE,"E120");Q1=makeQuery(id+"F28.imprint","IMPRINT",FACE,{"disambiguationData":[TD([[makeQuery(id+"F28.imprint","IMPRINT",EDGE,{"derivedFrom":subQ0}),-1.0]])]});}
            var Q2;
            {var subQ0=sQuery(id+"F28.wireOp",EDGE,"E121.MirrorCS");Q2=makeQuery(id+"F28.imprint","IMPRINT",FACE,{"disambiguationData":[TD([[makeQuery(id+"F28.imprint","IMPRINT",EDGE,{"derivedFrom":subQ0}),1.0]])]});}
            var Q3;
            {var subQ3=sQuery(id+"F28.wireOp",EDGE,"E122.MirrorCS");Q3=makeQuery(id+"F28.imprint","IMPRINT",FACE,{"disambiguationData":[TD([[makeQuery(id+"F28.imprint","IMPRINT",EDGE,{"derivedFrom":subQ3}),-1.0]])]});}
            var Q4;
            Q4=makeQuery(id+"F28.imprint","IMPRINT",FACE,{"disambiguationData":[TD([[makeQuery(id+"F28.imprint","IMPRINT",EDGE,{"derivedFrom":sQuery(id+"F28.wireOp",EDGE,"E116")}),-1.0]])]});
            extrude(context, id + "F29", {"entities" : qUnion([Q0, Q1, Q2, Q3, Q4]), "oppositeDirection" : true, "depth" : 2 * mm, "hasSecondDirection" : true, "secondDirectionOppositeDirection" : false, "secondDirectionDepth" : 4 * mm});
        }
        {
            var Q0;
            {var subQ0=sQuery(id+"F28.wireOp",EDGE,"E120");Q0=makeQuery(id+"F28.imprint","IMPRINT",FACE,{"disambiguationData":[TD([[makeQuery(id+"F28.imprint","IMPRINT",EDGE,{"derivedFrom":subQ0}),-1.0]])]});}
            var Q1;
            {var subQ0=sQuery(id+"F28.wireOp",EDGE,"E121.MirrorCS");Q1=makeQuery(id+"F28.imprint","IMPRINT",FACE,{"disambiguationData":[TD([[makeQuery(id+"F28.imprint","IMPRINT",EDGE,{"derivedFrom":subQ0}),1.0]])]});}
            var Q2;
            {var subQ3=sQuery(id+"F28.wireOp",EDGE,"E122.MirrorCS");Q2=makeQuery(id+"F28.imprint","IMPRINT",FACE,{"disambiguationData":[TD([[makeQuery(id+"F28.imprint","IMPRINT",EDGE,{"derivedFrom":subQ3}),-1.0]])]});}
            var Q3;
            Q3=makeQuery(id+"F28.imprint","IMPRINT",FACE,{"disambiguationData":[TD([[makeQuery(id+"F28.imprint","IMPRINT",EDGE,{"derivedFrom":sQuery(id+"F28.wireOp",EDGE,"E115")}),1.0]])]});
            extrude(context, id + "F30", {"entities" : qUnion([Q0, Q1, Q2, Q3]), "operationType" : NewBodyOperationType.ADD, "offsetDistance" : 25 * mm, "depth" : 15 * mm});
        }
        {
            var Q0;
            {var subQ0=sQuery(id+"F28.wireOp",EDGE,"E124.MirrorCS");Q0=makeQuery(id+"F30.boolean.opBoolean","MERGE",FACE,{"derivedFrom":[makeQuery(id+"F29.opExtrude","SWEPT_FACE",FACE,{"disambiguationData":[OSD([subQ0])]}),makeQuery(id+"F30.opExtrude","SWEPT_FACE",FACE,{"disambiguationData":[OSD([subQ0])]})]});}
            var sketch = newSketch(context, id + "F31", { "sketchPlane" : qUnion([Q0])});
            skLineSegment(sketch, "E125", {"start": v(-12, -4) * mm, "end": v(-12, 4) * mm, "construction": true});
            skPoint(sketch, "E126", {"position": v(-12, 0) * mm});
            skArc(sketch, "E127.0.startCap", {"start": v(-10.6, -4) * mm, "mid": v(-12, -5.4) * mm, "end": v(-13.4, -4) * mm, "construction": true});
            skArc(sketch, "E127.0.endCap", {"start": v(-13.4, 4) * mm, "mid": v(-12, 5.4) * mm, "end": v(-10.6, 4) * mm, "construction": true});
            skLineSegment(sketch, "E127.0.left", {"start": v(-13.4, -4) * mm, "end": v(-13.4, 4) * mm, "construction": true});
            skLineSegment(sketch, "E127.0.right", {"start": v(-10.6, -4) * mm, "end": v(-10.6, 4) * mm, "construction": true});
            skLineSegment(sketch, "E128.MirrorCS", {"start": v(10.6, -4) * mm, "end": v(10.6, 4) * mm, "construction": true});
            skArc(sketch, "E129.MirrorCS", {"start": v(13.4, 4) * mm, "mid": v(12, 5.4) * mm, "end": v(10.6, 4) * mm, "construction": true});
            skLineSegment(sketch, "E130.MirrorCS", {"start": v(13.4, -4) * mm, "end": v(13.4, 4) * mm, "construction": true});
            skArc(sketch, "E131.MirrorCS", {"start": v(10.6, -4) * mm, "mid": v(12, -5.4) * mm, "end": v(13.4, -4) * mm, "construction": true});
            skPoint(sketch, "E132.positionSnap0", {"position": v(-11.26, -18.6) * mm});
            skPoint(sketch, "E132.positionSnap1", {"position": v(-15.2, -10.1) * mm});
            skPoint(sketch, "E133", {"position": v(-12, -10.1) * mm});
            skLineSegment(sketch, "E134", {"start": v(-12, -10.1) * mm, "end": v(-12, -5.1) * mm, "construction": true});
            skLineSegment(sketch, "E135", {"start": v(-12, -10.1) * mm, "end": v(-12, -15.1) * mm, "construction": true});
            skLineSegment(sketch, "E136", {"start": v(-12, -5.1) * mm, "end": v(-12, -15.1) * mm, "construction": true});
            skArc(sketch, "E137.0.startCap", {"start": v(-13.4, -5.1) * mm, "mid": v(-12, -3.7) * mm, "end": v(-10.6, -5.1) * mm});
            skArc(sketch, "E137.0.endCap", {"start": v(-10.6, -15.1) * mm, "mid": v(-12, -16.5) * mm, "end": v(-13.4, -15.1) * mm});
            skLineSegment(sketch, "E137.0.left", {"start": v(-10.6, -5.1) * mm, "end": v(-10.6, -15.1) * mm});
            skLineSegment(sketch, "E137.0.right", {"start": v(-13.4, -5.1) * mm, "end": v(-13.4, -15.1) * mm});
            skArc(sketch, "E138.MirrorCS", {"start": v(10.6, -15.1) * mm, "mid": v(12, -16.5) * mm, "end": v(13.4, -15.1) * mm});
            skLineSegment(sketch, "E139.MirrorCS", {"start": v(10.6, -5.1) * mm, "end": v(10.6, -15.1) * mm});
            skArc(sketch, "E140.MirrorCS", {"start": v(13.4, -5.1) * mm, "mid": v(12, -3.7) * mm, "end": v(10.6, -5.1) * mm});
            skLineSegment(sketch, "E141.MirrorCS", {"start": v(13.4, -5.1) * mm, "end": v(13.4, -15.1) * mm});
            skSolve(sketch);
        }
        {
            var Q0;
            Q0=makeQuery(id+"F31.imprint","IMPRINT",FACE,{"disambiguationData":[TD([[makeQuery(id+"F31.imprint","IMPRINT",EDGE,{"derivedFrom":sQuery(id+"F31.wireOp",EDGE,"E137.0.startCap")}),-1.0]])]});
            var Q1;
            Q1=makeQuery(id+"F31.imprint","IMPRINT",FACE,{"disambiguationData":[TD([[makeQuery(id+"F31.imprint","IMPRINT",EDGE,{"derivedFrom":sQuery(id+"F31.wireOp",EDGE,"E138.MirrorCS")}),1.0]])]});
            extrude(context, id + "F32", {"entities" : qUnion([Q0, Q1]), "operationType" : NewBodyOperationType.REMOVE, "endBound" : BoundingType.UP_TO_NEXT, "oppositeDirection" : true, "offsetDistance" : 25 * mm, "depth" : 25 * mm});
        }
        {
            var Q0;
            Q0=makeQuery(id+"F29.opExtrude","CAP_FACE",FACE,{"disambiguationData":[OSD([sQuery(id+"F28.wireOp",EDGE,"E115"),sQuery(id+"F28.wireOp",EDGE,"E116"),sQuery(id+"F28.wireOp",EDGE,"E117.0"),sQuery(id+"F28.wireOp",EDGE,"E118"),sQuery(id+"F28.wireOp",EDGE,"E119"),sQuery(id+"F28.wireOp",EDGE,"E122.MirrorCS"),sQuery(id+"F28.wireOp",EDGE,"E123.MirrorCS"),sQuery(id+"F28.wireOp",EDGE,"E124.MirrorCS")])],"isStart":true});
            var sketch = newSketch(context, id + "F33", { "sketchPlane" : qUnion([Q0])});
            skCircle(sketch, "E142", {"center": v(0, 0) * mm, "radius": 5 * mm});
            skCircle(sketch, "E143", {"center": v(0, 0) * mm, "radius": 9.15 * mm});
            skSolve(sketch);
        }
        {
            var Q0;
            Q0=makeQuery(id+"F33.imprint","IMPRINT",FACE,{"disambiguationData":[TD([[makeQuery(id+"F33.imprint","IMPRINT",EDGE,{"derivedFrom":sQuery(id+"F33.wireOp",EDGE,"E142")}),-1.0]])]});
            var Q1;
            {var subQ0=sQuery(id+"F28.wireOp",EDGE,"E116");Q1=makeQuery(id+"F33.imprint","IMPRINT",FACE,{"disambiguationData":[TD([[makeQuery(id+"F33.imprint","IMPRINT",EDGE,{"derivedFrom":makeQuery(id+"F29.opExtrude","CAP_EDGE",EDGE,{"disambiguationData":[OSD([subQ0])],"isStart":true})}),-1.0]])]});}
            extrude(context, id + "F34", {"entities" : qUnion([Q0, Q1]), "operationType" : NewBodyOperationType.ADD, "oppositeDirection" : true, "depth" : 2 * mm});
        }
        {
            var Q0;
            Q0=makeQuery(id+"F2.opExtrude","SWEPT_FACE",FACE,{"disambiguationData":[OSD([sQuery(id+"F0.wireOp",EDGE,"E16.MirrorCS"),sQuery(id+"F0.wireOp",EDGE,"E17.MirrorCS")])]});
            var sketch = newSketch(context, id + "F35", { "sketchPlane" : qUnion([Q0])});
            skPoint(sketch, "E144.middle", {"position": v(0, 34) * mm});
            skCircle(sketch, "E145", {"center": v(0, 34) * mm, "radius": 8.5 * mm});
            skCircle(sketch, "E146", {"center": v(0, 34) * mm, "radius": 14 * mm});
            skLineSegment(sketch, "E147", {"start": v(-1.1, 34) * mm, "end": v(-1.1, 20.04) * mm});
            skLineSegment(sketch, "E148", {"start": v(1.1, 34) * mm, "end": v(1.1, 20.04) * mm});
            skLineSegment(sketch, "E149.1.0", {"start": v(-0.55, 33.05) * mm, "end": v(11.54, 26.07) * mm});
            skLineSegment(sketch, "E149.1.1", {"start": v(0.55, 34.95) * mm, "end": v(12.64, 27.97) * mm});
            skLineSegment(sketch, "E149.2.0", {"start": v(0.55, 33.05) * mm, "end": v(12.64, 40.03) * mm});
            skLineSegment(sketch, "E149.2.1", {"start": v(-0.55, 34.95) * mm, "end": v(11.54, 41.93) * mm});
            skLineSegment(sketch, "E149.3.0", {"start": v(1.1, 34) * mm, "end": v(1.1, 47.96) * mm});
            skLineSegment(sketch, "E149.3.1", {"start": v(-1.1, 34) * mm, "end": v(-1.1, 47.96) * mm});
            skLineSegment(sketch, "E149.4.0", {"start": v(0.55, 34.95) * mm, "end": v(-11.54, 41.93) * mm});
            skLineSegment(sketch, "E149.4.1", {"start": v(-0.55, 33.05) * mm, "end": v(-12.64, 40.03) * mm});
            skLineSegment(sketch, "E149.5.0", {"start": v(-0.55, 34.95) * mm, "end": v(-12.64, 27.97) * mm});
            skLineSegment(sketch, "E149.5.1", {"start": v(0.55, 33.05) * mm, "end": v(-11.54, 26.07) * mm});
            skLineSegment(sketch, "E150", {"start": v(-17, 48) * mm, "end": v(15.36, 48) * mm, "construction": true});
            skSolve(sketch);
        }
        {
            var Q0;
            {var subQ0=sQuery(id+"F35.wireOp",EDGE,"2794b337-0db7-454d-bffe-957635885cdd.filletArc");Q0=makeQuery(id+"F35.imprint","IMPRINT",FACE,{"disambiguationData":[TD([[makeQuery(id+"F35.imprint","IMPRINT",EDGE,{"derivedFrom":subQ0}),1.0]])]});}
            var Q1;
            {var subQ0=sQuery(id+"F35.wireOp",EDGE,"f5635e81-96b8-44ce-9882-6621aa2a2ab4.filletArc");Q1=makeQuery(id+"F35.imprint","IMPRINT",FACE,{"disambiguationData":[TD([[makeQuery(id+"F35.imprint","IMPRINT",EDGE,{"derivedFrom":subQ0}),1.0]])]});}
            var Q2;
            {var subQ5=sQuery(id+"F35.wireOp",EDGE,"fbe728dd-a97b-4c30-b279-c053e7003146.filletArc");Q2=makeQuery(id+"F35.imprint","IMPRINT",FACE,{"disambiguationData":[TD([[makeQuery(id+"F35.imprint","IMPRINT",EDGE,{"derivedFrom":subQ5}),1.0]])]});}
            var Q3;
            {var subQ5=sQuery(id+"F35.wireOp",EDGE,"1e11e860-624c-4577-b38d-3ad3859267b9.filletArc");Q3=makeQuery(id+"F35.imprint","IMPRINT",FACE,{"disambiguationData":[TD([[makeQuery(id+"F35.imprint","IMPRINT",EDGE,{"derivedFrom":subQ5}),1.0]])]});}
            var Q4;
            {var subQ0=sQuery(id+"F35.wireOp",EDGE,"E147");var subQ1=sQuery(id+"F35.wireOp",EDGE,"E145");var subQ2=makeQuery(id+"F35.imprint","INTERSECT",VERTEX,{"derivedFrom":[subQ1,subQ0]});Q4=makeQuery(id+"F35.imprint","IMPRINT",FACE,{"disambiguationData":[TD([[makeQuery(id+"F35.imprint","IMPRINT",EDGE,{"disambiguationData":[TD([[subQ2,1.0]])],"derivedFrom":subQ1}),-1.0]])]});}
            var Q5;
            {var subQ0=sQuery(id+"F35.wireOp",EDGE,"E148");var subQ1=sQuery(id+"F35.wireOp",EDGE,"E145");var subQ2=makeQuery(id+"F35.imprint","INTERSECT",VERTEX,{"derivedFrom":[subQ1,subQ0]});Q5=makeQuery(id+"F35.imprint","IMPRINT",FACE,{"disambiguationData":[TD([[makeQuery(id+"F35.imprint","IMPRINT",EDGE,{"disambiguationData":[TD([[subQ2,-1.0]])],"derivedFrom":subQ1}),-1.0]])]});}
            var Q6;
            {var subQ0=sQuery(id+"F35.wireOp",EDGE,"E149.2.0");var subQ1=sQuery(id+"F35.wireOp",EDGE,"E145");var subQ2=makeQuery(id+"F35.imprint","INTERSECT",VERTEX,{"derivedFrom":[subQ1,subQ0]});Q6=makeQuery(id+"F35.imprint","IMPRINT",FACE,{"disambiguationData":[TD([[makeQuery(id+"F35.imprint","IMPRINT",EDGE,{"disambiguationData":[TD([[subQ2,1.0]])],"derivedFrom":subQ1}),-1.0]])]});}
            var Q7;
            {var subQ0=sQuery(id+"F35.wireOp",EDGE,"E149.2.1");var subQ1=sQuery(id+"F35.wireOp",EDGE,"E145");var subQ2=makeQuery(id+"F35.imprint","INTERSECT",VERTEX,{"derivedFrom":[subQ1,subQ0]});Q7=makeQuery(id+"F35.imprint","IMPRINT",FACE,{"disambiguationData":[TD([[makeQuery(id+"F35.imprint","IMPRINT",EDGE,{"disambiguationData":[TD([[subQ2,-1.0]])],"derivedFrom":subQ1}),-1.0]])]});}
            var Q8;
            {var subQ0=sQuery(id+"F35.wireOp",EDGE,"E149.3.1");var subQ1=sQuery(id+"F35.wireOp",EDGE,"E145");var subQ2=makeQuery(id+"F35.imprint","INTERSECT",VERTEX,{"derivedFrom":[subQ1,subQ0]});Q8=makeQuery(id+"F35.imprint","IMPRINT",FACE,{"disambiguationData":[TD([[makeQuery(id+"F35.imprint","IMPRINT",EDGE,{"disambiguationData":[TD([[subQ2,-1.0]])],"derivedFrom":subQ1}),-1.0]])]});}
            var Q9;
            {var subQ0=sQuery(id+"F35.wireOp",EDGE,"E149.4.1");var subQ1=sQuery(id+"F35.wireOp",EDGE,"E145");var subQ2=makeQuery(id+"F35.imprint","INTERSECT",VERTEX,{"derivedFrom":[subQ1,subQ0]});Q9=makeQuery(id+"F35.imprint","IMPRINT",FACE,{"disambiguationData":[TD([[makeQuery(id+"F35.imprint","IMPRINT",EDGE,{"disambiguationData":[TD([[subQ2,-1.0]])],"derivedFrom":subQ1}),-1.0]])]});}
            extrude(context, id + "F36", {"entities" : qUnion([Q0, Q1, Q2, Q3, Q4, Q5, Q6, Q7, Q8, Q9]), "operationType" : NewBodyOperationType.REMOVE, "endBound" : BoundingType.UP_TO_NEXT, "oppositeDirection" : true, "depth" : 25 * mm});
        }
        {
            var Q0;
            Q0=makeQuery(id+"F36.boolean.opBoolean","COPY",EDGE,{"derivedFrom":makeQuery(id+"F36.opExtrude","SWEPT_EDGE",EDGE,{"disambiguationData":[OSD([sQuery(id+"F35.wireOp",EDGE,"E145"),sQuery(id+"F35.wireOp",EDGE,"E149.3.1")])]})});
            var Q1;
            Q1=makeQuery(id+"F36.boolean.opBoolean","COPY",EDGE,{"derivedFrom":makeQuery(id+"F36.opExtrude","SWEPT_EDGE",EDGE,{"disambiguationData":[OSD([sQuery(id+"F35.wireOp",EDGE,"E145"),sQuery(id+"F35.wireOp",EDGE,"E149.4.0")])]})});
            var Q2;
            Q2=makeQuery(id+"F36.boolean.opBoolean","COPY",EDGE,{"derivedFrom":makeQuery(id+"F36.opExtrude","SWEPT_EDGE",EDGE,{"disambiguationData":[OSD([sQuery(id+"F35.wireOp",EDGE,"E146"),sQuery(id+"F35.wireOp",EDGE,"E149.4.0")])]})});
            var Q3;
            Q3=makeQuery(id+"F36.boolean.opBoolean","COPY",EDGE,{"derivedFrom":makeQuery(id+"F36.opExtrude","SWEPT_EDGE",EDGE,{"disambiguationData":[OSD([sQuery(id+"F35.wireOp",EDGE,"E146"),sQuery(id+"F35.wireOp",EDGE,"E149.3.1")])]})});
            var Q4;
            Q4=makeQuery(id+"F36.boolean.opBoolean","COPY",EDGE,{"derivedFrom":makeQuery(id+"F36.opExtrude","SWEPT_EDGE",EDGE,{"disambiguationData":[OSD([sQuery(id+"F35.wireOp",EDGE,"E146"),sQuery(id+"F35.wireOp",EDGE,"E149.3.0")])]})});
            var Q5;
            Q5=makeQuery(id+"F36.boolean.opBoolean","COPY",EDGE,{"derivedFrom":makeQuery(id+"F36.opExtrude","SWEPT_EDGE",EDGE,{"disambiguationData":[OSD([sQuery(id+"F35.wireOp",EDGE,"E146"),sQuery(id+"F35.wireOp",EDGE,"E149.2.1")])]})});
            var Q6;
            Q6=makeQuery(id+"F36.boolean.opBoolean","COPY",EDGE,{"derivedFrom":makeQuery(id+"F36.opExtrude","SWEPT_EDGE",EDGE,{"disambiguationData":[OSD([sQuery(id+"F35.wireOp",EDGE,"E145"),sQuery(id+"F35.wireOp",EDGE,"E149.2.1")])]})});
            var Q7;
            Q7=makeQuery(id+"F36.boolean.opBoolean","COPY",EDGE,{"derivedFrom":makeQuery(id+"F36.opExtrude","SWEPT_EDGE",EDGE,{"disambiguationData":[OSD([sQuery(id+"F35.wireOp",EDGE,"E145"),sQuery(id+"F35.wireOp",EDGE,"E149.3.0")])]})});
            var Q8;
            Q8=makeQuery(id+"F36.boolean.opBoolean","COPY",EDGE,{"derivedFrom":makeQuery(id+"F36.opExtrude","SWEPT_EDGE",EDGE,{"disambiguationData":[OSD([sQuery(id+"F35.wireOp",EDGE,"E145"),sQuery(id+"F35.wireOp",EDGE,"E149.2.0")])]})});
            var Q9;
            Q9=makeQuery(id+"F36.boolean.opBoolean","COPY",EDGE,{"derivedFrom":makeQuery(id+"F36.opExtrude","SWEPT_EDGE",EDGE,{"disambiguationData":[OSD([sQuery(id+"F35.wireOp",EDGE,"E146"),sQuery(id+"F35.wireOp",EDGE,"E149.2.0")])]})});
            var Q10;
            Q10=makeQuery(id+"F36.boolean.opBoolean","COPY",EDGE,{"derivedFrom":makeQuery(id+"F36.opExtrude","SWEPT_EDGE",EDGE,{"disambiguationData":[OSD([sQuery(id+"F35.wireOp",EDGE,"E145"),sQuery(id+"F35.wireOp",EDGE,"E149.1.1")])]})});
            var Q11;
            Q11=makeQuery(id+"F36.boolean.opBoolean","COPY",EDGE,{"derivedFrom":makeQuery(id+"F36.opExtrude","SWEPT_EDGE",EDGE,{"disambiguationData":[OSD([sQuery(id+"F35.wireOp",EDGE,"E146"),sQuery(id+"F35.wireOp",EDGE,"E149.1.1")])]})});
            var Q12;
            Q12=makeQuery(id+"F36.boolean.opBoolean","COPY",EDGE,{"derivedFrom":makeQuery(id+"F36.opExtrude","SWEPT_EDGE",EDGE,{"disambiguationData":[OSD([sQuery(id+"F35.wireOp",EDGE,"E145"),sQuery(id+"F35.wireOp",EDGE,"E149.1.0")])]})});
            var Q13;
            Q13=makeQuery(id+"F36.boolean.opBoolean","COPY",EDGE,{"derivedFrom":makeQuery(id+"F36.opExtrude","SWEPT_EDGE",EDGE,{"disambiguationData":[OSD([sQuery(id+"F35.wireOp",EDGE,"E145"),sQuery(id+"F35.wireOp",EDGE,"E148")])]})});
            var Q14;
            Q14=makeQuery(id+"F36.boolean.opBoolean","COPY",EDGE,{"derivedFrom":makeQuery(id+"F36.opExtrude","SWEPT_EDGE",EDGE,{"disambiguationData":[OSD([sQuery(id+"F35.wireOp",EDGE,"E145"),sQuery(id+"F35.wireOp",EDGE,"E149.5.1")])]})});
            var Q15;
            Q15=makeQuery(id+"F36.boolean.opBoolean","COPY",EDGE,{"derivedFrom":makeQuery(id+"F36.opExtrude","SWEPT_EDGE",EDGE,{"disambiguationData":[OSD([sQuery(id+"F35.wireOp",EDGE,"E145"),sQuery(id+"F35.wireOp",EDGE,"E149.4.1")])]})});
            var Q16;
            Q16=makeQuery(id+"F36.boolean.opBoolean","COPY",EDGE,{"derivedFrom":makeQuery(id+"F36.opExtrude","SWEPT_EDGE",EDGE,{"disambiguationData":[OSD([sQuery(id+"F35.wireOp",EDGE,"E145"),sQuery(id+"F35.wireOp",EDGE,"E149.5.0")])]})});
            var Q17;
            Q17=makeQuery(id+"F36.boolean.opBoolean","COPY",EDGE,{"derivedFrom":makeQuery(id+"F36.opExtrude","SWEPT_EDGE",EDGE,{"disambiguationData":[OSD([sQuery(id+"F35.wireOp",EDGE,"E146"),sQuery(id+"F35.wireOp",EDGE,"E149.1.0")])]})});
            var Q18;
            Q18=makeQuery(id+"F36.boolean.opBoolean","COPY",EDGE,{"derivedFrom":makeQuery(id+"F36.opExtrude","SWEPT_EDGE",EDGE,{"disambiguationData":[OSD([sQuery(id+"F35.wireOp",EDGE,"E146"),sQuery(id+"F35.wireOp",EDGE,"E148")])]})});
            var Q19;
            Q19=makeQuery(id+"F36.boolean.opBoolean","COPY",EDGE,{"derivedFrom":makeQuery(id+"F36.opExtrude","SWEPT_EDGE",EDGE,{"disambiguationData":[OSD([sQuery(id+"F35.wireOp",EDGE,"E146"),sQuery(id+"F35.wireOp",EDGE,"E147")])]})});
            var Q20;
            Q20=makeQuery(id+"F36.boolean.opBoolean","COPY",EDGE,{"derivedFrom":makeQuery(id+"F36.opExtrude","SWEPT_EDGE",EDGE,{"disambiguationData":[OSD([sQuery(id+"F35.wireOp",EDGE,"E146"),sQuery(id+"F35.wireOp",EDGE,"E149.5.1")])]})});
            var Q21;
            Q21=makeQuery(id+"F36.boolean.opBoolean","COPY",EDGE,{"derivedFrom":makeQuery(id+"F36.opExtrude","SWEPT_EDGE",EDGE,{"disambiguationData":[OSD([sQuery(id+"F35.wireOp",EDGE,"E146"),sQuery(id+"F35.wireOp",EDGE,"E149.5.0")])]})});
            var Q22;
            Q22=makeQuery(id+"F36.boolean.opBoolean","COPY",EDGE,{"derivedFrom":makeQuery(id+"F36.opExtrude","SWEPT_EDGE",EDGE,{"disambiguationData":[OSD([sQuery(id+"F35.wireOp",EDGE,"E146"),sQuery(id+"F35.wireOp",EDGE,"E149.4.1")])]})});
            var Q23;
            Q23=makeQuery(id+"F36.boolean.opBoolean","COPY",EDGE,{"derivedFrom":makeQuery(id+"F36.opExtrude","SWEPT_EDGE",EDGE,{"disambiguationData":[OSD([sQuery(id+"F35.wireOp",EDGE,"E145"),sQuery(id+"F35.wireOp",EDGE,"E147")])]})});
            fillet(context, id + "F37", {"entities" : qUnion([Q0, Q1, Q2, Q3, Q4, Q5, Q6, Q7, Q8, Q9, Q10, Q11, Q12, Q13, Q14, Q15, Q16, Q17, Q18, Q19, Q20, Q21, Q22, Q23]), "radius" : 1 * mm, "tangentPropagation" : true, "allowEdgeOverflow" : false});
        }
    });
